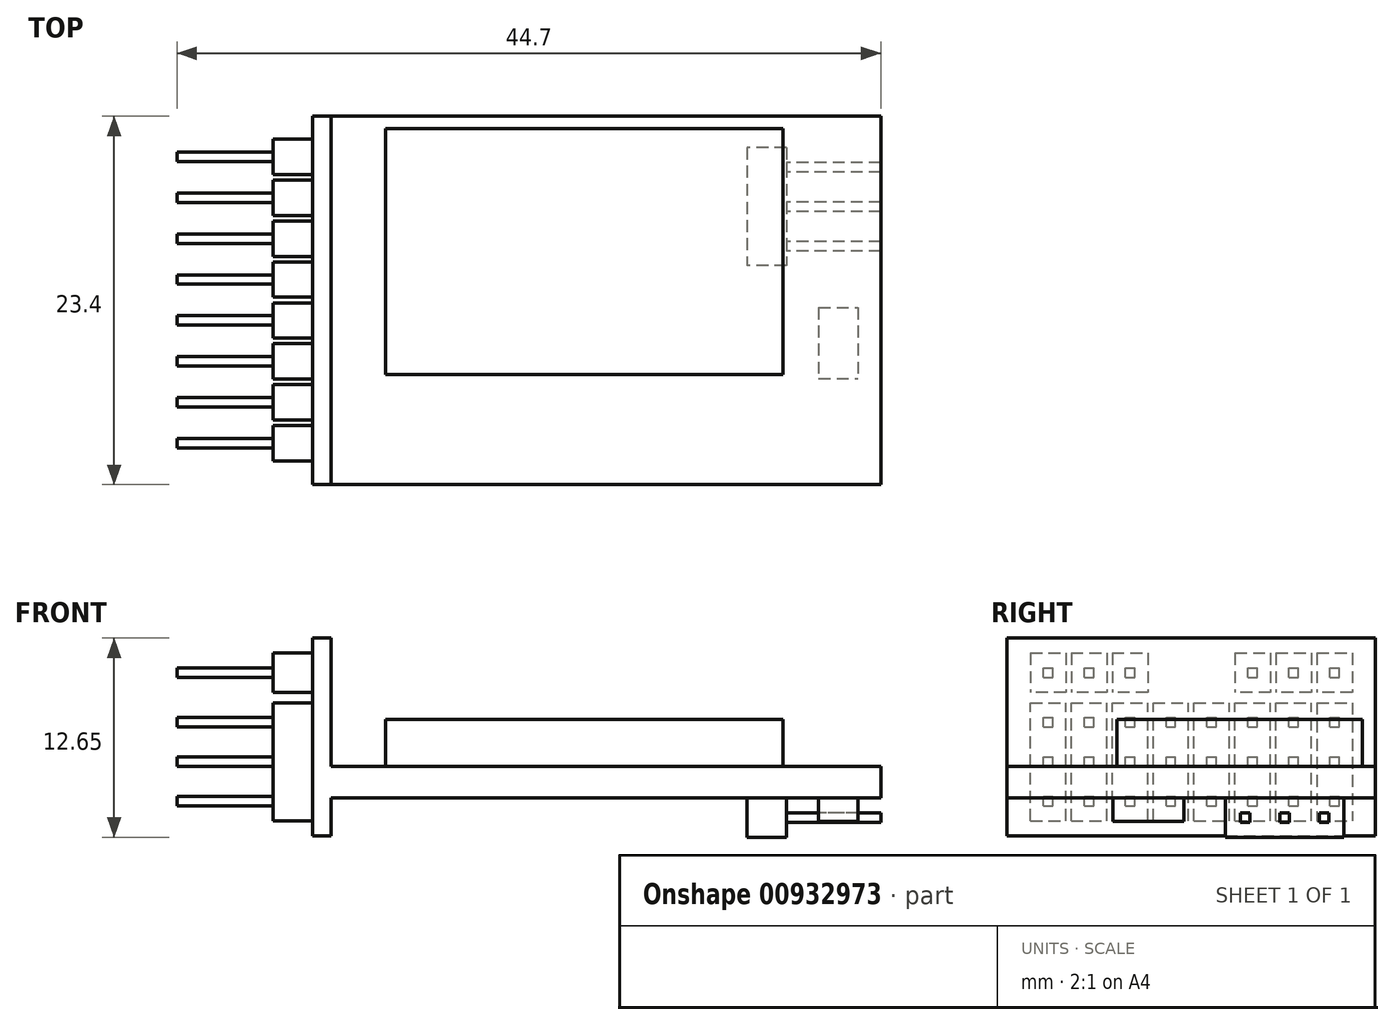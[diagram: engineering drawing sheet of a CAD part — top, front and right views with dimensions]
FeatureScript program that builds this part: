
annotation { "Feature Type Name" : "Feature", "Feature Type Description" : "" }
export const myFeature = defineFeature(function(context is Context, id is Id, definition is map)
    precondition{}
    {
        {
            var Q0;
            Q0=qCreatedBy(makeId("Top.planeOp"),FACE);
            var sketch = newSketch(context, id + "F0", { "sketchPlane" : qUnion([Q0])});
            skLineSegment(sketch, "E0.bottom", {"start": v(0, 0) * mm, "end": v(36.1, 0) * mm});
            skLineSegment(sketch, "E0.top", {"start": v(0, 23.4) * mm, "end": v(36.1, 23.4) * mm});
            skLineSegment(sketch, "E0.left", {"start": v(0, 0) * mm, "end": v(0, 23.4) * mm});
            skLineSegment(sketch, "E0.right", {"start": v(36.1, 0) * mm, "end": v(36.1, 23.4) * mm});
            skLineSegment(sketch, "E1.bottom", {"start": v(4.65, 22.6) * mm, "end": v(29.9, 22.6) * mm});
            skLineSegment(sketch, "E1.top", {"start": v(4.65, 7) * mm, "end": v(29.9, 7) * mm});
            skLineSegment(sketch, "E1.left", {"start": v(4.65, 22.6) * mm, "end": v(4.65, 7) * mm});
            skLineSegment(sketch, "E1.right", {"start": v(29.9, 22.6) * mm, "end": v(29.9, 7) * mm});
            skSolve(sketch);
        }
        {
            var Q0;
            Q0=makeQuery(id+"F0.imprint","IMPRINT",FACE,{"disambiguationData":[TD([[makeQuery(id+"F0.imprint","IMPRINT",EDGE,{"derivedFrom":sQuery(id+"F0.wireOp",EDGE,"E0.bottom")}),1.0]])]});
            extrude(context, id + "F1", {"entities" : qUnion([Q0]), "depth" : 2 * mm, "offsetDistance" : 25 * mm});
        }
        {
            var Q0;
            Q0=makeQuery(id+"F1.opExtrude","SWEPT_FACE",FACE,{"disambiguationData":[OSD([sQuery(id+"F0.wireOp",EDGE,"E0.left")])]});
            var sketch = newSketch(context, id + "F2", { "sketchPlane" : qUnion([Q0])});
            skLineSegment(sketch, "E2.bottom", {"start": v(0, -2.4) * mm, "end": v(-23.4, -2.4) * mm});
            skLineSegment(sketch, "E2.top", {"start": v(0, 10.15) * mm, "end": v(-23.4, 10.15) * mm});
            skLineSegment(sketch, "E2.left", {"start": v(0, -2.4) * mm, "end": v(0, 10.15) * mm});
            skLineSegment(sketch, "E2.right", {"start": v(-23.4, -2.4) * mm, "end": v(-23.4, 10.15) * mm});
            skPoint(sketch, "E3.0", {"position": v(0, 2) * mm});
            skPoint(sketch, "E4.0", {"position": v(0, 0) * mm});
            skLineSegment(sketch, "E5", {"start": v(-11.7, 10.15) * mm, "end": v(-11.7, -2.4) * mm, "construction": true});
            skLineSegment(sketch, "E6.bottom", {"start": v(-1.45, 9.2) * mm, "end": v(-21.95, 9.2) * mm});
            skLineSegment(sketch, "E6.top", {"start": v(-1.45, -1.45) * mm, "end": v(-21.95, -1.45) * mm});
            skLineSegment(sketch, "E6.left", {"start": v(-1.45, 9.2) * mm, "end": v(-1.45, -1.45) * mm});
            skLineSegment(sketch, "E6.right", {"start": v(-21.95, 9.2) * mm, "end": v(-21.95, -1.45) * mm});
            skPoint(sketch, "E6.middle", {"position": v(-11.7, 3.87) * mm});
            skLineSegment(sketch, "E7", {"start": v(-19.7, 9.2) * mm, "end": v(-19.7, -1.45) * mm});
            skLineSegment(sketch, "E8.bottom", {"start": v(-21.95, 9.2) * mm, "end": v(-19.7, 9.2) * mm});
            skLineSegment(sketch, "E8.top", {"start": v(-21.95, 6.2) * mm, "end": v(-19.7, 6.2) * mm});
            skLineSegment(sketch, "E8.left", {"start": v(-21.95, 9.2) * mm, "end": v(-21.95, 6.2) * mm});
            skLineSegment(sketch, "E8.right", {"start": v(-19.7, 9.2) * mm, "end": v(-19.7, 6.2) * mm});
            skLineSegment(sketch, "E9.bottom", {"start": v(-19.7, -1.45) * mm, "end": v(-21.95, -1.45) * mm});
            skLineSegment(sketch, "E9.top", {"start": v(-19.7, 1.05) * mm, "end": v(-21.95, 1.05) * mm});
            skLineSegment(sketch, "E9.left", {"start": v(-19.7, -1.45) * mm, "end": v(-19.7, 1.05) * mm});
            skLineSegment(sketch, "E9.right", {"start": v(-21.95, -1.45) * mm, "end": v(-21.95, 1.05) * mm});
            skLineSegment(sketch, "E10.top", {"start": v(-19.7, 3.55) * mm, "end": v(-21.95, 3.55) * mm});
            skLineSegment(sketch, "E10.left", {"start": v(-19.7, 1.05) * mm, "end": v(-19.7, 3.55) * mm});
            skLineSegment(sketch, "E10.right", {"start": v(-21.95, 1.05) * mm, "end": v(-21.95, 3.55) * mm});
            skLineSegment(sketch, "E11.top", {"start": v(-19.7, 6.05) * mm, "end": v(-21.95, 6.05) * mm});
            skLineSegment(sketch, "E11.left", {"start": v(-19.7, 3.55) * mm, "end": v(-19.7, 6.05) * mm});
            skLineSegment(sketch, "E11.right", {"start": v(-21.95, 3.55) * mm, "end": v(-21.95, 6.05) * mm});
            skLineSegment(sketch, "E12.top", {"start": v(-21.95, 6.7) * mm, "end": v(-19.7, 6.7) * mm});
            skLineSegment(sketch, "E12.left", {"start": v(-21.95, 9.2) * mm, "end": v(-21.95, 6.7) * mm});
            skLineSegment(sketch, "E12.right", {"start": v(-19.7, 9.2) * mm, "end": v(-19.7, 6.7) * mm});
            skLineSegment(sketch, "E13", {"start": v(-20.83, 9.2) * mm, "end": v(-20.83, 6.7) * mm, "construction": true});
            skLineSegment(sketch, "E14", {"start": v(-20.83, 6.05) * mm, "end": v(-20.83, 3.55) * mm, "construction": true});
            skLineSegment(sketch, "E15", {"start": v(-20.83, 3.55) * mm, "end": v(-20.83, 1.05) * mm, "construction": true});
            skLineSegment(sketch, "E16", {"start": v(-20.83, 1.05) * mm, "end": v(-20.83, -1.45) * mm, "construction": true});
            skLineSegment(sketch, "E17.bottom", {"start": v(-20.53, 4.5) * mm, "end": v(-21.13, 4.5) * mm});
            skLineSegment(sketch, "E17.top", {"start": v(-20.53, 5.1) * mm, "end": v(-21.13, 5.1) * mm});
            skLineSegment(sketch, "E17.left", {"start": v(-20.53, 4.5) * mm, "end": v(-20.53, 5.1) * mm});
            skLineSegment(sketch, "E17.right", {"start": v(-21.13, 4.5) * mm, "end": v(-21.13, 5.1) * mm});
            skPoint(sketch, "E17.middle", {"position": v(-20.83, 4.8) * mm});
            skLineSegment(sketch, "E18.bottom", {"start": v(-20.53, 2) * mm, "end": v(-21.13, 2) * mm});
            skLineSegment(sketch, "E18.top", {"start": v(-20.53, 2.6) * mm, "end": v(-21.13, 2.6) * mm});
            skLineSegment(sketch, "E18.left", {"start": v(-20.53, 2) * mm, "end": v(-20.53, 2.6) * mm});
            skLineSegment(sketch, "E18.right", {"start": v(-21.13, 2) * mm, "end": v(-21.13, 2.6) * mm});
            skPoint(sketch, "E18.middle", {"position": v(-20.83, 2.3) * mm});
            skLineSegment(sketch, "E19.bottom", {"start": v(-20.53, -0.5) * mm, "end": v(-21.13, -0.5) * mm});
            skLineSegment(sketch, "E19.top", {"start": v(-20.53, 0.1) * mm, "end": v(-21.13, 0.1) * mm});
            skLineSegment(sketch, "E19.left", {"start": v(-20.53, -0.5) * mm, "end": v(-20.53, 0.1) * mm});
            skLineSegment(sketch, "E19.right", {"start": v(-21.13, -0.5) * mm, "end": v(-21.13, 0.1) * mm});
            skPoint(sketch, "E19.middle", {"position": v(-20.83, -0.2) * mm});
            skLineSegment(sketch, "E20.bottom", {"start": v(-20.53, 7.65) * mm, "end": v(-21.13, 7.65) * mm});
            skLineSegment(sketch, "E20.top", {"start": v(-20.53, 8.25) * mm, "end": v(-21.13, 8.25) * mm});
            skLineSegment(sketch, "E20.left", {"start": v(-20.53, 7.65) * mm, "end": v(-20.53, 8.25) * mm});
            skLineSegment(sketch, "E20.right", {"start": v(-21.13, 7.65) * mm, "end": v(-21.13, 8.25) * mm});
            skPoint(sketch, "E20.middle", {"position": v(-20.83, 7.95) * mm});
            skLineSegment(sketch, "E21.1.0.0", {"start": v(-17.1, 9.2) * mm, "end": v(-17.1, 6.7) * mm});
            skLineSegment(sketch, "E21.1.0.1", {"start": v(-17.1, 1.05) * mm, "end": v(-17.1, 3.55) * mm});
            skLineSegment(sketch, "E21.1.0.2", {"start": v(-18.23, 9.2) * mm, "end": v(-18.23, 6.7) * mm, "construction": true});
            skLineSegment(sketch, "E21.1.0.3", {"start": v(-18.22, 3.55) * mm, "end": v(-18.22, 1.05) * mm, "construction": true});
            skLineSegment(sketch, "E21.1.0.4", {"start": v(-18.22, 1.05) * mm, "end": v(-18.22, -1.45) * mm, "construction": true});
            skLineSegment(sketch, "E21.1.0.5", {"start": v(-17.1, 3.55) * mm, "end": v(-19.35, 3.55) * mm});
            skPoint(sketch, "E21.1.0.6", {"position": v(-18.22, 2.3) * mm});
            skLineSegment(sketch, "E21.1.0.7", {"start": v(-19.35, 3.55) * mm, "end": v(-19.35, 6.05) * mm});
            skLineSegment(sketch, "E21.1.0.8", {"start": v(-17.1, 1.05) * mm, "end": v(-19.35, 1.05) * mm});
            skLineSegment(sketch, "E21.1.0.9", {"start": v(-19.35, 6.2) * mm, "end": v(-17.1, 6.2) * mm});
            skLineSegment(sketch, "E21.1.0.10", {"start": v(-18.22, 6.05) * mm, "end": v(-18.22, 3.55) * mm, "construction": true});
            skPoint(sketch, "E21.1.0.11", {"position": v(-18.22, -0.2) * mm});
            skPoint(sketch, "E21.1.0.12", {"position": v(-18.22, 7.95) * mm});
            skLineSegment(sketch, "E21.1.0.13", {"start": v(-17.1, 3.55) * mm, "end": v(-17.1, 6.05) * mm});
            skLineSegment(sketch, "E21.1.0.14", {"start": v(-19.35, 9.2) * mm, "end": v(-17.1, 9.2) * mm});
            skLineSegment(sketch, "E21.1.0.15", {"start": v(-19.35, 6.7) * mm, "end": v(-17.1, 6.7) * mm});
            skLineSegment(sketch, "E21.1.0.16", {"start": v(-19.35, 9.2) * mm, "end": v(-19.35, 6.7) * mm});
            skLineSegment(sketch, "E21.1.0.17", {"start": v(-19.35, -1.45) * mm, "end": v(-19.35, 1.05) * mm});
            skLineSegment(sketch, "E21.1.0.18", {"start": v(-19.35, 1.05) * mm, "end": v(-19.35, 3.55) * mm});
            skLineSegment(sketch, "E21.1.0.19", {"start": v(-17.1, -1.45) * mm, "end": v(-17.1, 1.05) * mm});
            skLineSegment(sketch, "E21.1.0.20", {"start": v(-17.1, -1.45) * mm, "end": v(-19.35, -1.45) * mm});
            skLineSegment(sketch, "E21.1.0.21", {"start": v(-17.1, 6.05) * mm, "end": v(-19.35, 6.05) * mm});
            skPoint(sketch, "E21.1.0.22", {"position": v(-18.22, 4.8) * mm});
            skLineSegment(sketch, "E21.1.0.23", {"start": v(-17.1, 9.2) * mm, "end": v(-17.1, -1.45) * mm});
            skLineSegment(sketch, "E21.1.0.24", {"start": v(-17.1, 9.2) * mm, "end": v(-17.1, 6.2) * mm});
            skLineSegment(sketch, "E21.1.0.25", {"start": v(-19.35, 9.2) * mm, "end": v(-19.35, -1.45) * mm});
            skLineSegment(sketch, "E21.1.0.26", {"start": v(-19.35, 9.2) * mm, "end": v(-19.35, 6.2) * mm});
            skLineSegment(sketch, "E21.1.0.27", {"start": v(-17.1, 1.05) * mm, "end": v(-19.35, 1.05) * mm});
            skLineSegment(sketch, "E21.1.0.28", {"start": v(-17.1, 3.55) * mm, "end": v(-19.35, 3.55) * mm});
            skLineSegment(sketch, "E21.1.0.29", {"start": v(-19.35, 9.2) * mm, "end": v(-17.1, 9.2) * mm});
            skLineSegment(sketch, "E21.1.0.30", {"start": v(-17.93, 2) * mm, "end": v(-18.53, 2) * mm});
            skLineSegment(sketch, "E21.1.0.31", {"start": v(-18.52, 4.5) * mm, "end": v(-18.52, 5.1) * mm});
            skLineSegment(sketch, "E21.1.0.32", {"start": v(-17.93, 2.6) * mm, "end": v(-18.53, 2.6) * mm});
            skLineSegment(sketch, "E21.1.0.33", {"start": v(-17.93, -0.5) * mm, "end": v(-18.52, -0.5) * mm});
            skLineSegment(sketch, "E21.1.0.34", {"start": v(-17.93, 7.65) * mm, "end": v(-17.93, 8.25) * mm});
            skLineSegment(sketch, "E21.1.0.35", {"start": v(-17.93, 2) * mm, "end": v(-17.93, 2.6) * mm});
            skLineSegment(sketch, "E21.1.0.36", {"start": v(-18.52, -0.5) * mm, "end": v(-18.52, 0.1) * mm});
            skLineSegment(sketch, "E21.1.0.37", {"start": v(-17.93, -0.5) * mm, "end": v(-17.93, 0.1) * mm});
            skLineSegment(sketch, "E21.1.0.38", {"start": v(-17.93, 7.65) * mm, "end": v(-18.52, 7.65) * mm});
            skLineSegment(sketch, "E21.1.0.39", {"start": v(-18.53, 2) * mm, "end": v(-18.53, 2.6) * mm});
            skLineSegment(sketch, "E21.1.0.40", {"start": v(-18.52, 7.65) * mm, "end": v(-18.52, 8.25) * mm});
            skLineSegment(sketch, "E21.1.0.41", {"start": v(-17.93, 4.5) * mm, "end": v(-18.52, 4.5) * mm});
            skLineSegment(sketch, "E21.1.0.42", {"start": v(-17.93, 5.1) * mm, "end": v(-18.52, 5.1) * mm});
            skLineSegment(sketch, "E21.1.0.43", {"start": v(-17.93, 8.25) * mm, "end": v(-18.52, 8.25) * mm});
            skLineSegment(sketch, "E21.1.0.44", {"start": v(-17.93, 4.5) * mm, "end": v(-17.93, 5.1) * mm});
            skLineSegment(sketch, "E21.1.0.45", {"start": v(-17.93, 0.1) * mm, "end": v(-18.52, 0.1) * mm});
            skLineSegment(sketch, "E21.2.0.0", {"start": v(-14.5, 9.2) * mm, "end": v(-14.5, 6.7) * mm});
            skLineSegment(sketch, "E21.2.0.1", {"start": v(-14.5, 1.05) * mm, "end": v(-14.5, 3.55) * mm});
            skLineSegment(sketch, "E21.2.0.2", {"start": v(-15.63, 9.2) * mm, "end": v(-15.63, 6.7) * mm, "construction": true});
            skLineSegment(sketch, "E21.2.0.3", {"start": v(-15.62, 3.55) * mm, "end": v(-15.62, 1.05) * mm, "construction": true});
            skLineSegment(sketch, "E21.2.0.4", {"start": v(-15.62, 1.05) * mm, "end": v(-15.62, -1.45) * mm, "construction": true});
            skLineSegment(sketch, "E21.2.0.5", {"start": v(-14.5, 3.55) * mm, "end": v(-16.75, 3.55) * mm});
            skPoint(sketch, "E21.2.0.6", {"position": v(-15.62, 2.3) * mm});
            skLineSegment(sketch, "E21.2.0.7", {"start": v(-16.75, 3.55) * mm, "end": v(-16.75, 6.05) * mm});
            skLineSegment(sketch, "E21.2.0.8", {"start": v(-14.5, 1.05) * mm, "end": v(-16.75, 1.05) * mm});
            skLineSegment(sketch, "E21.2.0.9", {"start": v(-16.75, 6.2) * mm, "end": v(-14.5, 6.2) * mm});
            skLineSegment(sketch, "E21.2.0.10", {"start": v(-15.62, 6.05) * mm, "end": v(-15.62, 3.55) * mm, "construction": true});
            skPoint(sketch, "E21.2.0.11", {"position": v(-15.62, -0.2) * mm});
            skPoint(sketch, "E21.2.0.12", {"position": v(-15.62, 7.95) * mm});
            skLineSegment(sketch, "E21.2.0.13", {"start": v(-14.5, 3.55) * mm, "end": v(-14.5, 6.05) * mm});
            skLineSegment(sketch, "E21.2.0.14", {"start": v(-16.75, 9.2) * mm, "end": v(-14.5, 9.2) * mm});
            skLineSegment(sketch, "E21.2.0.15", {"start": v(-16.75, 6.7) * mm, "end": v(-14.5, 6.7) * mm});
            skLineSegment(sketch, "E21.2.0.16", {"start": v(-16.75, 9.2) * mm, "end": v(-16.75, 6.7) * mm});
            skLineSegment(sketch, "E21.2.0.17", {"start": v(-16.75, -1.45) * mm, "end": v(-16.75, 1.05) * mm});
            skLineSegment(sketch, "E21.2.0.18", {"start": v(-16.75, 1.05) * mm, "end": v(-16.75, 3.55) * mm});
            skLineSegment(sketch, "E21.2.0.19", {"start": v(-14.5, -1.45) * mm, "end": v(-14.5, 1.05) * mm});
            skLineSegment(sketch, "E21.2.0.20", {"start": v(-14.5, -1.45) * mm, "end": v(-16.75, -1.45) * mm});
            skLineSegment(sketch, "E21.2.0.21", {"start": v(-14.5, 6.05) * mm, "end": v(-16.75, 6.05) * mm});
            skPoint(sketch, "E21.2.0.22", {"position": v(-15.62, 4.8) * mm});
            skLineSegment(sketch, "E21.2.0.23", {"start": v(-14.5, 9.2) * mm, "end": v(-14.5, -1.45) * mm});
            skLineSegment(sketch, "E21.2.0.24", {"start": v(-14.5, 9.2) * mm, "end": v(-14.5, 6.2) * mm});
            skLineSegment(sketch, "E21.2.0.25", {"start": v(-16.75, 9.2) * mm, "end": v(-16.75, -1.45) * mm});
            skLineSegment(sketch, "E21.2.0.26", {"start": v(-16.75, 9.2) * mm, "end": v(-16.75, 6.2) * mm});
            skLineSegment(sketch, "E21.2.0.27", {"start": v(-14.5, 1.05) * mm, "end": v(-16.75, 1.05) * mm});
            skLineSegment(sketch, "E21.2.0.28", {"start": v(-14.5, 3.55) * mm, "end": v(-16.75, 3.55) * mm});
            skLineSegment(sketch, "E21.2.0.29", {"start": v(-16.75, 9.2) * mm, "end": v(-14.5, 9.2) * mm});
            skLineSegment(sketch, "E21.2.0.30", {"start": v(-15.33, 2) * mm, "end": v(-15.93, 2) * mm});
            skLineSegment(sketch, "E21.2.0.31", {"start": v(-15.93, 4.5) * mm, "end": v(-15.93, 5.1) * mm});
            skLineSegment(sketch, "E21.2.0.32", {"start": v(-15.33, 2.6) * mm, "end": v(-15.93, 2.6) * mm});
            skLineSegment(sketch, "E21.2.0.33", {"start": v(-15.33, -0.5) * mm, "end": v(-15.93, -0.5) * mm});
            skLineSegment(sketch, "E21.2.0.34", {"start": v(-15.33, 7.65) * mm, "end": v(-15.33, 8.25) * mm});
            skLineSegment(sketch, "E21.2.0.35", {"start": v(-15.33, 2) * mm, "end": v(-15.33, 2.6) * mm});
            skLineSegment(sketch, "E21.2.0.36", {"start": v(-15.93, -0.5) * mm, "end": v(-15.93, 0.1) * mm});
            skLineSegment(sketch, "E21.2.0.37", {"start": v(-15.33, -0.5) * mm, "end": v(-15.33, 0.1) * mm});
            skLineSegment(sketch, "E21.2.0.38", {"start": v(-15.33, 7.65) * mm, "end": v(-15.93, 7.65) * mm});
            skLineSegment(sketch, "E21.2.0.39", {"start": v(-15.93, 2) * mm, "end": v(-15.93, 2.6) * mm});
            skLineSegment(sketch, "E21.2.0.40", {"start": v(-15.93, 7.65) * mm, "end": v(-15.93, 8.25) * mm});
            skLineSegment(sketch, "E21.2.0.41", {"start": v(-15.33, 4.5) * mm, "end": v(-15.93, 4.5) * mm});
            skLineSegment(sketch, "E21.2.0.42", {"start": v(-15.33, 5.1) * mm, "end": v(-15.93, 5.1) * mm});
            skLineSegment(sketch, "E21.2.0.43", {"start": v(-15.33, 8.25) * mm, "end": v(-15.93, 8.25) * mm});
            skLineSegment(sketch, "E21.2.0.44", {"start": v(-15.33, 4.5) * mm, "end": v(-15.33, 5.1) * mm});
            skLineSegment(sketch, "E21.2.0.45", {"start": v(-15.33, 0.1) * mm, "end": v(-15.93, 0.1) * mm});
            skLineSegment(sketch, "E21.3.0.0", {"start": v(-11.9, 9.2) * mm, "end": v(-11.9, 6.7) * mm});
            skLineSegment(sketch, "E21.3.0.1", {"start": v(-11.9, 1.05) * mm, "end": v(-11.9, 3.55) * mm});
            skLineSegment(sketch, "E21.3.0.2", {"start": v(-13.03, 9.2) * mm, "end": v(-13.03, 6.7) * mm, "construction": true});
            skLineSegment(sketch, "E21.3.0.3", {"start": v(-13.02, 3.55) * mm, "end": v(-13.02, 1.05) * mm, "construction": true});
            skLineSegment(sketch, "E21.3.0.4", {"start": v(-13.02, 1.05) * mm, "end": v(-13.02, -1.45) * mm, "construction": true});
            skLineSegment(sketch, "E21.3.0.5", {"start": v(-11.9, 3.55) * mm, "end": v(-14.15, 3.55) * mm});
            skPoint(sketch, "E21.3.0.6", {"position": v(-13.02, 2.3) * mm});
            skLineSegment(sketch, "E21.3.0.7", {"start": v(-14.15, 3.55) * mm, "end": v(-14.15, 6.05) * mm});
            skLineSegment(sketch, "E21.3.0.8", {"start": v(-11.9, 1.05) * mm, "end": v(-14.15, 1.05) * mm});
            skLineSegment(sketch, "E21.3.0.9", {"start": v(-14.15, 6.2) * mm, "end": v(-11.9, 6.2) * mm});
            skLineSegment(sketch, "E21.3.0.10", {"start": v(-13.02, 6.05) * mm, "end": v(-13.02, 3.55) * mm, "construction": true});
            skPoint(sketch, "E21.3.0.11", {"position": v(-13.02, -0.2) * mm});
            skPoint(sketch, "E21.3.0.12", {"position": v(-13.02, 7.95) * mm});
            skLineSegment(sketch, "E21.3.0.13", {"start": v(-11.9, 3.55) * mm, "end": v(-11.9, 6.05) * mm});
            skLineSegment(sketch, "E21.3.0.14", {"start": v(-14.15, 9.2) * mm, "end": v(-11.9, 9.2) * mm});
            skLineSegment(sketch, "E21.3.0.15", {"start": v(-14.15, 6.7) * mm, "end": v(-11.9, 6.7) * mm});
            skLineSegment(sketch, "E21.3.0.16", {"start": v(-14.15, 9.2) * mm, "end": v(-14.15, 6.7) * mm});
            skLineSegment(sketch, "E21.3.0.17", {"start": v(-14.15, -1.45) * mm, "end": v(-14.15, 1.05) * mm});
            skLineSegment(sketch, "E21.3.0.18", {"start": v(-14.15, 1.05) * mm, "end": v(-14.15, 3.55) * mm});
            skLineSegment(sketch, "E21.3.0.19", {"start": v(-11.9, -1.45) * mm, "end": v(-11.9, 1.05) * mm});
            skLineSegment(sketch, "E21.3.0.20", {"start": v(-11.9, -1.45) * mm, "end": v(-14.15, -1.45) * mm});
            skLineSegment(sketch, "E21.3.0.21", {"start": v(-11.9, 6.05) * mm, "end": v(-14.15, 6.05) * mm});
            skPoint(sketch, "E21.3.0.22", {"position": v(-13.02, 4.8) * mm});
            skLineSegment(sketch, "E21.3.0.23", {"start": v(-11.9, 9.2) * mm, "end": v(-11.9, -1.45) * mm});
            skLineSegment(sketch, "E21.3.0.24", {"start": v(-11.9, 9.2) * mm, "end": v(-11.9, 6.2) * mm});
            skLineSegment(sketch, "E21.3.0.25", {"start": v(-14.15, 9.2) * mm, "end": v(-14.15, -1.45) * mm});
            skLineSegment(sketch, "E21.3.0.26", {"start": v(-14.15, 9.2) * mm, "end": v(-14.15, 6.2) * mm});
            skLineSegment(sketch, "E21.3.0.27", {"start": v(-11.9, 1.05) * mm, "end": v(-14.15, 1.05) * mm});
            skLineSegment(sketch, "E21.3.0.28", {"start": v(-11.9, 3.55) * mm, "end": v(-14.15, 3.55) * mm});
            skLineSegment(sketch, "E21.3.0.29", {"start": v(-14.15, 9.2) * mm, "end": v(-11.9, 9.2) * mm});
            skLineSegment(sketch, "E21.3.0.30", {"start": v(-12.73, 2) * mm, "end": v(-13.33, 2) * mm});
            skLineSegment(sketch, "E21.3.0.31", {"start": v(-13.32, 4.5) * mm, "end": v(-13.32, 5.1) * mm});
            skLineSegment(sketch, "E21.3.0.32", {"start": v(-12.73, 2.6) * mm, "end": v(-13.33, 2.6) * mm});
            skLineSegment(sketch, "E21.3.0.33", {"start": v(-12.72, -0.5) * mm, "end": v(-13.32, -0.5) * mm});
            skLineSegment(sketch, "E21.3.0.34", {"start": v(-12.72, 7.65) * mm, "end": v(-12.72, 8.25) * mm});
            skLineSegment(sketch, "E21.3.0.35", {"start": v(-12.73, 2) * mm, "end": v(-12.73, 2.6) * mm});
            skLineSegment(sketch, "E21.3.0.36", {"start": v(-13.32, -0.5) * mm, "end": v(-13.32, 0.1) * mm});
            skLineSegment(sketch, "E21.3.0.37", {"start": v(-12.72, -0.5) * mm, "end": v(-12.72, 0.1) * mm});
            skLineSegment(sketch, "E21.3.0.38", {"start": v(-12.72, 7.65) * mm, "end": v(-13.32, 7.65) * mm});
            skLineSegment(sketch, "E21.3.0.39", {"start": v(-13.33, 2) * mm, "end": v(-13.33, 2.6) * mm});
            skLineSegment(sketch, "E21.3.0.40", {"start": v(-13.32, 7.65) * mm, "end": v(-13.32, 8.25) * mm});
            skLineSegment(sketch, "E21.3.0.41", {"start": v(-12.72, 4.5) * mm, "end": v(-13.32, 4.5) * mm});
            skLineSegment(sketch, "E21.3.0.42", {"start": v(-12.72, 5.1) * mm, "end": v(-13.32, 5.1) * mm});
            skLineSegment(sketch, "E21.3.0.43", {"start": v(-12.72, 8.25) * mm, "end": v(-13.32, 8.25) * mm});
            skLineSegment(sketch, "E21.3.0.44", {"start": v(-12.72, 4.5) * mm, "end": v(-12.72, 5.1) * mm});
            skLineSegment(sketch, "E21.3.0.45", {"start": v(-12.72, 0.1) * mm, "end": v(-13.32, 0.1) * mm});
            skLineSegment(sketch, "E21.4.0.0", {"start": v(-9.3, 9.2) * mm, "end": v(-9.3, 6.7) * mm});
            skLineSegment(sketch, "E21.4.0.1", {"start": v(-9.3, 1.05) * mm, "end": v(-9.3, 3.55) * mm});
            skLineSegment(sketch, "E21.4.0.2", {"start": v(-10.43, 9.2) * mm, "end": v(-10.43, 6.7) * mm, "construction": true});
            skLineSegment(sketch, "E21.4.0.3", {"start": v(-10.42, 3.55) * mm, "end": v(-10.42, 1.05) * mm, "construction": true});
            skLineSegment(sketch, "E21.4.0.4", {"start": v(-10.42, 1.05) * mm, "end": v(-10.42, -1.45) * mm, "construction": true});
            skLineSegment(sketch, "E21.4.0.5", {"start": v(-9.3, 3.55) * mm, "end": v(-11.55, 3.55) * mm});
            skPoint(sketch, "E21.4.0.6", {"position": v(-10.42, 2.3) * mm});
            skLineSegment(sketch, "E21.4.0.7", {"start": v(-11.55, 3.55) * mm, "end": v(-11.55, 6.05) * mm});
            skLineSegment(sketch, "E21.4.0.8", {"start": v(-9.3, 1.05) * mm, "end": v(-11.55, 1.05) * mm});
            skLineSegment(sketch, "E21.4.0.9", {"start": v(-11.55, 6.2) * mm, "end": v(-9.3, 6.2) * mm});
            skLineSegment(sketch, "E21.4.0.10", {"start": v(-10.42, 6.05) * mm, "end": v(-10.42, 3.55) * mm, "construction": true});
            skPoint(sketch, "E21.4.0.11", {"position": v(-10.42, -0.2) * mm});
            skPoint(sketch, "E21.4.0.12", {"position": v(-10.42, 7.95) * mm});
            skLineSegment(sketch, "E21.4.0.13", {"start": v(-9.3, 3.55) * mm, "end": v(-9.3, 6.05) * mm});
            skLineSegment(sketch, "E21.4.0.14", {"start": v(-11.55, 9.2) * mm, "end": v(-9.3, 9.2) * mm});
            skLineSegment(sketch, "E21.4.0.15", {"start": v(-11.55, 6.7) * mm, "end": v(-9.3, 6.7) * mm});
            skLineSegment(sketch, "E21.4.0.16", {"start": v(-11.55, 9.2) * mm, "end": v(-11.55, 6.7) * mm});
            skLineSegment(sketch, "E21.4.0.17", {"start": v(-11.55, -1.45) * mm, "end": v(-11.55, 1.05) * mm});
            skLineSegment(sketch, "E21.4.0.18", {"start": v(-11.55, 1.05) * mm, "end": v(-11.55, 3.55) * mm});
            skLineSegment(sketch, "E21.4.0.19", {"start": v(-9.3, -1.45) * mm, "end": v(-9.3, 1.05) * mm});
            skLineSegment(sketch, "E21.4.0.20", {"start": v(-9.3, -1.45) * mm, "end": v(-11.55, -1.45) * mm});
            skLineSegment(sketch, "E21.4.0.21", {"start": v(-9.3, 6.05) * mm, "end": v(-11.55, 6.05) * mm});
            skPoint(sketch, "E21.4.0.22", {"position": v(-10.42, 4.8) * mm});
            skLineSegment(sketch, "E21.4.0.23", {"start": v(-9.3, 9.2) * mm, "end": v(-9.3, -1.45) * mm});
            skLineSegment(sketch, "E21.4.0.24", {"start": v(-9.3, 9.2) * mm, "end": v(-9.3, 6.2) * mm});
            skLineSegment(sketch, "E21.4.0.25", {"start": v(-11.55, 9.2) * mm, "end": v(-11.55, -1.45) * mm});
            skLineSegment(sketch, "E21.4.0.26", {"start": v(-11.55, 9.2) * mm, "end": v(-11.55, 6.2) * mm});
            skLineSegment(sketch, "E21.4.0.27", {"start": v(-9.3, 1.05) * mm, "end": v(-11.55, 1.05) * mm});
            skLineSegment(sketch, "E21.4.0.28", {"start": v(-9.3, 3.55) * mm, "end": v(-11.55, 3.55) * mm});
            skLineSegment(sketch, "E21.4.0.29", {"start": v(-11.55, 9.2) * mm, "end": v(-9.3, 9.2) * mm});
            skLineSegment(sketch, "E21.4.0.30", {"start": v(-10.13, 2) * mm, "end": v(-10.73, 2) * mm});
            skLineSegment(sketch, "E21.4.0.31", {"start": v(-10.72, 4.5) * mm, "end": v(-10.72, 5.1) * mm});
            skLineSegment(sketch, "E21.4.0.32", {"start": v(-10.13, 2.6) * mm, "end": v(-10.73, 2.6) * mm});
            skLineSegment(sketch, "E21.4.0.33", {"start": v(-10.12, -0.5) * mm, "end": v(-10.72, -0.5) * mm});
            skLineSegment(sketch, "E21.4.0.34", {"start": v(-10.12, 7.65) * mm, "end": v(-10.12, 8.25) * mm});
            skLineSegment(sketch, "E21.4.0.35", {"start": v(-10.13, 2) * mm, "end": v(-10.13, 2.6) * mm});
            skLineSegment(sketch, "E21.4.0.36", {"start": v(-10.72, -0.5) * mm, "end": v(-10.72, 0.1) * mm});
            skLineSegment(sketch, "E21.4.0.37", {"start": v(-10.12, -0.5) * mm, "end": v(-10.12, 0.1) * mm});
            skLineSegment(sketch, "E21.4.0.38", {"start": v(-10.12, 7.65) * mm, "end": v(-10.72, 7.65) * mm});
            skLineSegment(sketch, "E21.4.0.39", {"start": v(-10.73, 2) * mm, "end": v(-10.73, 2.6) * mm});
            skLineSegment(sketch, "E21.4.0.40", {"start": v(-10.72, 7.65) * mm, "end": v(-10.72, 8.25) * mm});
            skLineSegment(sketch, "E21.4.0.41", {"start": v(-10.12, 4.5) * mm, "end": v(-10.72, 4.5) * mm});
            skLineSegment(sketch, "E21.4.0.42", {"start": v(-10.12, 5.1) * mm, "end": v(-10.72, 5.1) * mm});
            skLineSegment(sketch, "E21.4.0.43", {"start": v(-10.12, 8.25) * mm, "end": v(-10.72, 8.25) * mm});
            skLineSegment(sketch, "E21.4.0.44", {"start": v(-10.12, 4.5) * mm, "end": v(-10.12, 5.1) * mm});
            skLineSegment(sketch, "E21.4.0.45", {"start": v(-10.12, 0.1) * mm, "end": v(-10.72, 0.1) * mm});
            skLineSegment(sketch, "E21.5.0.0", {"start": v(-6.7, 9.2) * mm, "end": v(-6.7, 6.7) * mm});
            skLineSegment(sketch, "E21.5.0.1", {"start": v(-6.7, 1.05) * mm, "end": v(-6.7, 3.55) * mm});
            skLineSegment(sketch, "E21.5.0.2", {"start": v(-7.83, 9.2) * mm, "end": v(-7.83, 6.7) * mm, "construction": true});
            skLineSegment(sketch, "E21.5.0.3", {"start": v(-7.82, 3.55) * mm, "end": v(-7.82, 1.05) * mm, "construction": true});
            skLineSegment(sketch, "E21.5.0.4", {"start": v(-7.82, 1.05) * mm, "end": v(-7.82, -1.45) * mm, "construction": true});
            skLineSegment(sketch, "E21.5.0.5", {"start": v(-6.7, 3.55) * mm, "end": v(-8.95, 3.55) * mm});
            skPoint(sketch, "E21.5.0.6", {"position": v(-7.82, 2.3) * mm});
            skLineSegment(sketch, "E21.5.0.7", {"start": v(-8.95, 3.55) * mm, "end": v(-8.95, 6.05) * mm});
            skLineSegment(sketch, "E21.5.0.8", {"start": v(-6.7, 1.05) * mm, "end": v(-8.95, 1.05) * mm});
            skLineSegment(sketch, "E21.5.0.9", {"start": v(-8.95, 6.2) * mm, "end": v(-6.7, 6.2) * mm});
            skLineSegment(sketch, "E21.5.0.10", {"start": v(-7.82, 6.05) * mm, "end": v(-7.82, 3.55) * mm, "construction": true});
            skPoint(sketch, "E21.5.0.11", {"position": v(-7.82, -0.2) * mm});
            skPoint(sketch, "E21.5.0.12", {"position": v(-7.82, 7.95) * mm});
            skLineSegment(sketch, "E21.5.0.13", {"start": v(-6.7, 3.55) * mm, "end": v(-6.7, 6.05) * mm});
            skLineSegment(sketch, "E21.5.0.14", {"start": v(-8.95, 9.2) * mm, "end": v(-6.7, 9.2) * mm});
            skLineSegment(sketch, "E21.5.0.15", {"start": v(-8.95, 6.7) * mm, "end": v(-6.7, 6.7) * mm});
            skLineSegment(sketch, "E21.5.0.16", {"start": v(-8.95, 9.2) * mm, "end": v(-8.95, 6.7) * mm});
            skLineSegment(sketch, "E21.5.0.17", {"start": v(-8.95, -1.45) * mm, "end": v(-8.95, 1.05) * mm});
            skLineSegment(sketch, "E21.5.0.18", {"start": v(-8.95, 1.05) * mm, "end": v(-8.95, 3.55) * mm});
            skLineSegment(sketch, "E21.5.0.19", {"start": v(-6.7, -1.45) * mm, "end": v(-6.7, 1.05) * mm});
            skLineSegment(sketch, "E21.5.0.20", {"start": v(-6.7, -1.45) * mm, "end": v(-8.95, -1.45) * mm});
            skLineSegment(sketch, "E21.5.0.21", {"start": v(-6.7, 6.05) * mm, "end": v(-8.95, 6.05) * mm});
            skPoint(sketch, "E21.5.0.22", {"position": v(-7.82, 4.8) * mm});
            skLineSegment(sketch, "E21.5.0.23", {"start": v(-6.7, 9.2) * mm, "end": v(-6.7, -1.45) * mm});
            skLineSegment(sketch, "E21.5.0.24", {"start": v(-6.7, 9.2) * mm, "end": v(-6.7, 6.2) * mm});
            skLineSegment(sketch, "E21.5.0.25", {"start": v(-8.95, 9.2) * mm, "end": v(-8.95, -1.45) * mm});
            skLineSegment(sketch, "E21.5.0.26", {"start": v(-8.95, 9.2) * mm, "end": v(-8.95, 6.2) * mm});
            skLineSegment(sketch, "E21.5.0.27", {"start": v(-6.7, 1.05) * mm, "end": v(-8.95, 1.05) * mm});
            skLineSegment(sketch, "E21.5.0.28", {"start": v(-6.7, 3.55) * mm, "end": v(-8.95, 3.55) * mm});
            skLineSegment(sketch, "E21.5.0.29", {"start": v(-8.95, 9.2) * mm, "end": v(-6.7, 9.2) * mm});
            skLineSegment(sketch, "E21.5.0.30", {"start": v(-7.53, 2) * mm, "end": v(-8.13, 2) * mm});
            skLineSegment(sketch, "E21.5.0.31", {"start": v(-8.12, 4.5) * mm, "end": v(-8.12, 5.1) * mm});
            skLineSegment(sketch, "E21.5.0.32", {"start": v(-7.53, 2.6) * mm, "end": v(-8.13, 2.6) * mm});
            skLineSegment(sketch, "E21.5.0.33", {"start": v(-7.53, -0.5) * mm, "end": v(-8.12, -0.5) * mm});
            skLineSegment(sketch, "E21.5.0.34", {"start": v(-7.53, 7.65) * mm, "end": v(-7.53, 8.25) * mm});
            skLineSegment(sketch, "E21.5.0.35", {"start": v(-7.53, 2) * mm, "end": v(-7.53, 2.6) * mm});
            skLineSegment(sketch, "E21.5.0.36", {"start": v(-8.12, -0.5) * mm, "end": v(-8.12, 0.1) * mm});
            skLineSegment(sketch, "E21.5.0.37", {"start": v(-7.53, -0.5) * mm, "end": v(-7.53, 0.1) * mm});
            skLineSegment(sketch, "E21.5.0.38", {"start": v(-7.53, 7.65) * mm, "end": v(-8.12, 7.65) * mm});
            skLineSegment(sketch, "E21.5.0.39", {"start": v(-8.13, 2) * mm, "end": v(-8.13, 2.6) * mm});
            skLineSegment(sketch, "E21.5.0.40", {"start": v(-8.12, 7.65) * mm, "end": v(-8.12, 8.25) * mm});
            skLineSegment(sketch, "E21.5.0.41", {"start": v(-7.53, 4.5) * mm, "end": v(-8.12, 4.5) * mm});
            skLineSegment(sketch, "E21.5.0.42", {"start": v(-7.53, 5.1) * mm, "end": v(-8.12, 5.1) * mm});
            skLineSegment(sketch, "E21.5.0.43", {"start": v(-7.53, 8.25) * mm, "end": v(-8.12, 8.25) * mm});
            skLineSegment(sketch, "E21.5.0.44", {"start": v(-7.53, 4.5) * mm, "end": v(-7.53, 5.1) * mm});
            skLineSegment(sketch, "E21.5.0.45", {"start": v(-7.53, 0.1) * mm, "end": v(-8.12, 0.1) * mm});
            skLineSegment(sketch, "E21.6.0.0", {"start": v(-4.1, 9.2) * mm, "end": v(-4.1, 6.7) * mm});
            skLineSegment(sketch, "E21.6.0.1", {"start": v(-4.1, 1.05) * mm, "end": v(-4.1, 3.55) * mm});
            skLineSegment(sketch, "E21.6.0.2", {"start": v(-5.23, 9.2) * mm, "end": v(-5.23, 6.7) * mm, "construction": true});
            skLineSegment(sketch, "E21.6.0.3", {"start": v(-5.22, 3.55) * mm, "end": v(-5.22, 1.05) * mm, "construction": true});
            skLineSegment(sketch, "E21.6.0.4", {"start": v(-5.22, 1.05) * mm, "end": v(-5.22, -1.45) * mm, "construction": true});
            skLineSegment(sketch, "E21.6.0.5", {"start": v(-4.1, 3.55) * mm, "end": v(-6.35, 3.55) * mm});
            skPoint(sketch, "E21.6.0.6", {"position": v(-5.22, 2.3) * mm});
            skLineSegment(sketch, "E21.6.0.7", {"start": v(-6.35, 3.55) * mm, "end": v(-6.35, 6.05) * mm});
            skLineSegment(sketch, "E21.6.0.8", {"start": v(-4.1, 1.05) * mm, "end": v(-6.35, 1.05) * mm});
            skLineSegment(sketch, "E21.6.0.9", {"start": v(-6.35, 6.2) * mm, "end": v(-4.1, 6.2) * mm});
            skLineSegment(sketch, "E21.6.0.10", {"start": v(-5.22, 6.05) * mm, "end": v(-5.22, 3.55) * mm, "construction": true});
            skPoint(sketch, "E21.6.0.11", {"position": v(-5.22, -0.2) * mm});
            skPoint(sketch, "E21.6.0.12", {"position": v(-5.22, 7.95) * mm});
            skLineSegment(sketch, "E21.6.0.13", {"start": v(-4.1, 3.55) * mm, "end": v(-4.1, 6.05) * mm});
            skLineSegment(sketch, "E21.6.0.14", {"start": v(-6.35, 9.2) * mm, "end": v(-4.1, 9.2) * mm});
            skLineSegment(sketch, "E21.6.0.15", {"start": v(-6.35, 6.7) * mm, "end": v(-4.1, 6.7) * mm});
            skLineSegment(sketch, "E21.6.0.16", {"start": v(-6.35, 9.2) * mm, "end": v(-6.35, 6.7) * mm});
            skLineSegment(sketch, "E21.6.0.17", {"start": v(-6.35, -1.45) * mm, "end": v(-6.35, 1.05) * mm});
            skLineSegment(sketch, "E21.6.0.18", {"start": v(-6.35, 1.05) * mm, "end": v(-6.35, 3.55) * mm});
            skLineSegment(sketch, "E21.6.0.19", {"start": v(-4.1, -1.45) * mm, "end": v(-4.1, 1.05) * mm});
            skLineSegment(sketch, "E21.6.0.20", {"start": v(-4.1, -1.45) * mm, "end": v(-6.35, -1.45) * mm});
            skLineSegment(sketch, "E21.6.0.21", {"start": v(-4.1, 6.05) * mm, "end": v(-6.35, 6.05) * mm});
            skPoint(sketch, "E21.6.0.22", {"position": v(-5.22, 4.8) * mm});
            skLineSegment(sketch, "E21.6.0.23", {"start": v(-4.1, 9.2) * mm, "end": v(-4.1, -1.45) * mm});
            skLineSegment(sketch, "E21.6.0.24", {"start": v(-4.1, 9.2) * mm, "end": v(-4.1, 6.2) * mm});
            skLineSegment(sketch, "E21.6.0.25", {"start": v(-6.35, 9.2) * mm, "end": v(-6.35, -1.45) * mm});
            skLineSegment(sketch, "E21.6.0.26", {"start": v(-6.35, 9.2) * mm, "end": v(-6.35, 6.2) * mm});
            skLineSegment(sketch, "E21.6.0.27", {"start": v(-4.1, 1.05) * mm, "end": v(-6.35, 1.05) * mm});
            skLineSegment(sketch, "E21.6.0.28", {"start": v(-4.1, 3.55) * mm, "end": v(-6.35, 3.55) * mm});
            skLineSegment(sketch, "E21.6.0.29", {"start": v(-6.35, 9.2) * mm, "end": v(-4.1, 9.2) * mm});
            skLineSegment(sketch, "E21.6.0.30", {"start": v(-4.93, 2) * mm, "end": v(-5.53, 2) * mm});
            skLineSegment(sketch, "E21.6.0.31", {"start": v(-5.52, 4.5) * mm, "end": v(-5.52, 5.1) * mm});
            skLineSegment(sketch, "E21.6.0.32", {"start": v(-4.93, 2.6) * mm, "end": v(-5.53, 2.6) * mm});
            skLineSegment(sketch, "E21.6.0.33", {"start": v(-4.93, -0.5) * mm, "end": v(-5.52, -0.5) * mm});
            skLineSegment(sketch, "E21.6.0.34", {"start": v(-4.92, 7.65) * mm, "end": v(-4.92, 8.25) * mm});
            skLineSegment(sketch, "E21.6.0.35", {"start": v(-4.93, 2) * mm, "end": v(-4.93, 2.6) * mm});
            skLineSegment(sketch, "E21.6.0.36", {"start": v(-5.52, -0.5) * mm, "end": v(-5.52, 0.1) * mm});
            skLineSegment(sketch, "E21.6.0.37", {"start": v(-4.92, -0.5) * mm, "end": v(-4.92, 0.1) * mm});
            skLineSegment(sketch, "E21.6.0.38", {"start": v(-4.93, 7.65) * mm, "end": v(-5.52, 7.65) * mm});
            skLineSegment(sketch, "E21.6.0.39", {"start": v(-5.53, 2) * mm, "end": v(-5.53, 2.6) * mm});
            skLineSegment(sketch, "E21.6.0.40", {"start": v(-5.52, 7.65) * mm, "end": v(-5.52, 8.25) * mm});
            skLineSegment(sketch, "E21.6.0.41", {"start": v(-4.92, 4.5) * mm, "end": v(-5.52, 4.5) * mm});
            skLineSegment(sketch, "E21.6.0.42", {"start": v(-4.92, 5.1) * mm, "end": v(-5.52, 5.1) * mm});
            skLineSegment(sketch, "E21.6.0.43", {"start": v(-4.92, 8.25) * mm, "end": v(-5.52, 8.25) * mm});
            skLineSegment(sketch, "E21.6.0.44", {"start": v(-4.92, 4.5) * mm, "end": v(-4.92, 5.1) * mm});
            skLineSegment(sketch, "E21.6.0.45", {"start": v(-4.92, 0.1) * mm, "end": v(-5.52, 0.1) * mm});
            skLineSegment(sketch, "E21.7.0.0", {"start": v(-1.5, 9.2) * mm, "end": v(-1.5, 6.7) * mm});
            skLineSegment(sketch, "E21.7.0.1", {"start": v(-1.5, 1.05) * mm, "end": v(-1.5, 3.55) * mm});
            skLineSegment(sketch, "E21.7.0.2", {"start": v(-2.63, 9.2) * mm, "end": v(-2.63, 6.7) * mm, "construction": true});
            skLineSegment(sketch, "E21.7.0.3", {"start": v(-2.62, 3.55) * mm, "end": v(-2.62, 1.05) * mm, "construction": true});
            skLineSegment(sketch, "E21.7.0.4", {"start": v(-2.62, 1.05) * mm, "end": v(-2.62, -1.45) * mm, "construction": true});
            skLineSegment(sketch, "E21.7.0.5", {"start": v(-1.5, 3.55) * mm, "end": v(-3.75, 3.55) * mm});
            skPoint(sketch, "E21.7.0.6", {"position": v(-2.62, 2.3) * mm});
            skLineSegment(sketch, "E21.7.0.7", {"start": v(-3.75, 3.55) * mm, "end": v(-3.75, 6.05) * mm});
            skLineSegment(sketch, "E21.7.0.8", {"start": v(-1.5, 1.05) * mm, "end": v(-3.75, 1.05) * mm});
            skLineSegment(sketch, "E21.7.0.9", {"start": v(-3.75, 6.2) * mm, "end": v(-1.5, 6.2) * mm});
            skLineSegment(sketch, "E21.7.0.10", {"start": v(-2.62, 6.05) * mm, "end": v(-2.62, 3.55) * mm, "construction": true});
            skPoint(sketch, "E21.7.0.11", {"position": v(-2.62, -0.2) * mm});
            skPoint(sketch, "E21.7.0.12", {"position": v(-2.62, 7.95) * mm});
            skLineSegment(sketch, "E21.7.0.13", {"start": v(-1.5, 3.55) * mm, "end": v(-1.5, 6.05) * mm});
            skLineSegment(sketch, "E21.7.0.14", {"start": v(-3.75, 9.2) * mm, "end": v(-1.5, 9.2) * mm});
            skLineSegment(sketch, "E21.7.0.15", {"start": v(-3.75, 6.7) * mm, "end": v(-1.5, 6.7) * mm});
            skLineSegment(sketch, "E21.7.0.16", {"start": v(-3.75, 9.2) * mm, "end": v(-3.75, 6.7) * mm});
            skLineSegment(sketch, "E21.7.0.17", {"start": v(-3.75, -1.45) * mm, "end": v(-3.75, 1.05) * mm});
            skLineSegment(sketch, "E21.7.0.18", {"start": v(-3.75, 1.05) * mm, "end": v(-3.75, 3.55) * mm});
            skLineSegment(sketch, "E21.7.0.19", {"start": v(-1.5, -1.45) * mm, "end": v(-1.5, 1.05) * mm});
            skLineSegment(sketch, "E21.7.0.20", {"start": v(-1.5, -1.45) * mm, "end": v(-3.75, -1.45) * mm});
            skLineSegment(sketch, "E21.7.0.21", {"start": v(-1.5, 6.05) * mm, "end": v(-3.75, 6.05) * mm});
            skPoint(sketch, "E21.7.0.22", {"position": v(-2.62, 4.8) * mm});
            skLineSegment(sketch, "E21.7.0.23", {"start": v(-1.5, 9.2) * mm, "end": v(-1.5, -1.45) * mm});
            skLineSegment(sketch, "E21.7.0.24", {"start": v(-1.5, 9.2) * mm, "end": v(-1.5, 6.2) * mm});
            skLineSegment(sketch, "E21.7.0.25", {"start": v(-3.75, 9.2) * mm, "end": v(-3.75, -1.45) * mm});
            skLineSegment(sketch, "E21.7.0.26", {"start": v(-3.75, 9.2) * mm, "end": v(-3.75, 6.2) * mm});
            skLineSegment(sketch, "E21.7.0.27", {"start": v(-1.5, 1.05) * mm, "end": v(-3.75, 1.05) * mm});
            skLineSegment(sketch, "E21.7.0.28", {"start": v(-1.5, 3.55) * mm, "end": v(-3.75, 3.55) * mm});
            skLineSegment(sketch, "E21.7.0.29", {"start": v(-3.75, 9.2) * mm, "end": v(-1.5, 9.2) * mm});
            skLineSegment(sketch, "E21.7.0.30", {"start": v(-2.33, 2) * mm, "end": v(-2.93, 2) * mm});
            skLineSegment(sketch, "E21.7.0.31", {"start": v(-2.93, 4.5) * mm, "end": v(-2.93, 5.1) * mm});
            skLineSegment(sketch, "E21.7.0.32", {"start": v(-2.33, 2.6) * mm, "end": v(-2.93, 2.6) * mm});
            skLineSegment(sketch, "E21.7.0.33", {"start": v(-2.33, -0.5) * mm, "end": v(-2.93, -0.5) * mm});
            skLineSegment(sketch, "E21.7.0.34", {"start": v(-2.33, 7.65) * mm, "end": v(-2.33, 8.25) * mm});
            skLineSegment(sketch, "E21.7.0.35", {"start": v(-2.33, 2) * mm, "end": v(-2.33, 2.6) * mm});
            skLineSegment(sketch, "E21.7.0.36", {"start": v(-2.93, -0.5) * mm, "end": v(-2.93, 0.1) * mm});
            skLineSegment(sketch, "E21.7.0.37", {"start": v(-2.33, -0.5) * mm, "end": v(-2.33, 0.1) * mm});
            skLineSegment(sketch, "E21.7.0.38", {"start": v(-2.33, 7.65) * mm, "end": v(-2.93, 7.65) * mm});
            skLineSegment(sketch, "E21.7.0.39", {"start": v(-2.93, 2) * mm, "end": v(-2.93, 2.6) * mm});
            skLineSegment(sketch, "E21.7.0.40", {"start": v(-2.93, 7.65) * mm, "end": v(-2.93, 8.25) * mm});
            skLineSegment(sketch, "E21.7.0.41", {"start": v(-2.33, 4.5) * mm, "end": v(-2.93, 4.5) * mm});
            skLineSegment(sketch, "E21.7.0.42", {"start": v(-2.33, 5.1) * mm, "end": v(-2.93, 5.1) * mm});
            skLineSegment(sketch, "E21.7.0.43", {"start": v(-2.33, 8.25) * mm, "end": v(-2.93, 8.25) * mm});
            skLineSegment(sketch, "E21.7.0.44", {"start": v(-2.33, 4.5) * mm, "end": v(-2.33, 5.1) * mm});
            skLineSegment(sketch, "E21.7.0.45", {"start": v(-2.33, 0.1) * mm, "end": v(-2.93, 0.1) * mm});
            skLineSegment(sketch, "E21.direction1", {"start": v(-21.95, -1.45) * mm, "end": v(-19.35, -1.45) * mm, "construction": true});
            skSolve(sketch);
        }
        {
            var Q0;
            {var subQ27=sQuery(id+"F2.wireOp",EDGE,"E2.top");Q0=makeQuery(id+"F2.imprint","IMPRINT",FACE,{"disambiguationData":[TD([[makeQuery(id+"F2.imprint","IMPRINT",EDGE,{"derivedFrom":subQ27}),1.0]])]});}
            var Q1;
            {var subQ27=sQuery(id+"F2.wireOp",EDGE,"E2.bottom");Q1=makeQuery(id+"F2.imprint","IMPRINT",FACE,{"disambiguationData":[TD([[makeQuery(id+"F2.imprint","IMPRINT",EDGE,{"derivedFrom":subQ27}),-1.0]])]});}
            var Q2;
            {var subQ1=sQuery(id+"F2.wireOp",EDGE,"E10.top");Q2=makeQuery(id+"F2.imprint","IMPRINT",FACE,{"disambiguationData":[TD([[makeQuery(id+"F2.imprint","IMPRINT",EDGE,{"derivedFrom":subQ1}),-1.0]])]});}
            var Q3;
            {var subQ10=sQuery(id+"F2.wireOp",EDGE,"E21.1.0.7");Q3=makeQuery(id+"F2.imprint","IMPRINT",FACE,{"disambiguationData":[TD([[makeQuery(id+"F2.imprint","IMPRINT",EDGE,{"derivedFrom":subQ10}),1.0]])]});}
            var Q4;
            {var subQ0=sQuery(id+"F2.wireOp",EDGE,"E21.7.0.33");Q4=makeQuery(id+"F2.imprint","IMPRINT",FACE,{"disambiguationData":[TD([[makeQuery(id+"F2.imprint","IMPRINT",EDGE,{"derivedFrom":subQ0}),1.0]])]});}
            var Q5;
            {var subQ0=sQuery(id+"F2.wireOp",EDGE,"E21.5.0.19");var subQ1=sQuery(id+"F2.wireOp",EDGE,"E6.top");var subQ2=makeQuery(id+"F2.imprint","INTERSECT",VERTEX,{"derivedFrom":[subQ1,subQ0]});Q5=makeQuery(id+"F2.imprint","IMPRINT",FACE,{"disambiguationData":[TD([[makeQuery(id+"F2.imprint","IMPRINT",EDGE,{"disambiguationData":[TD([[subQ2,1.0]])],"derivedFrom":subQ1}),-1.0]])]});}
            var Q6;
            {var subQ3=sQuery(id+"F0.wireOp",EDGE,"E0.left");var subQ4=makeQuery(id+"F1.opExtrude","CAP_EDGE",EDGE,{"disambiguationData":[OSD([subQ3])],"isStart":true});var subQ6=sQuery(id+"F2.wireOp",EDGE,"E21.6.0.19");var subQ9=makeQuery(id+"F2.imprint","INTERSECT",VERTEX,{"derivedFrom":[subQ4,subQ6]});Q6=makeQuery(id+"F2.imprint","IMPRINT",FACE,{"disambiguationData":[TD([[makeQuery(id+"F2.imprint","IMPRINT",EDGE,{"disambiguationData":[TD([[subQ9,1.0]])],"derivedFrom":subQ4}),-1.0]])]});}
            var Q7;
            {var subQ3=sQuery(id+"F0.wireOp",EDGE,"E0.left");var subQ4=makeQuery(id+"F1.opExtrude","CAP_EDGE",EDGE,{"disambiguationData":[OSD([subQ3])],"isStart":true});var subQ6=sQuery(id+"F2.wireOp",EDGE,"E21.2.0.19");var subQ9=makeQuery(id+"F2.imprint","INTERSECT",VERTEX,{"derivedFrom":[subQ4,subQ6]});Q7=makeQuery(id+"F2.imprint","IMPRINT",FACE,{"disambiguationData":[TD([[makeQuery(id+"F2.imprint","IMPRINT",EDGE,{"disambiguationData":[TD([[subQ9,1.0]])],"derivedFrom":subQ4}),-1.0]])]});}
            var Q8;
            {var subQ1=sQuery(id+"F2.wireOp",EDGE,"E21.4.0.8");Q8=makeQuery(id+"F2.imprint","IMPRINT",FACE,{"disambiguationData":[TD([[makeQuery(id+"F2.imprint","IMPRINT",EDGE,{"derivedFrom":subQ1}),-1.0]])]});}
            var Q9;
            {var subQ0=sQuery(id+"F2.wireOp",EDGE,"E21.6.0.19");var subQ1=sQuery(id+"F2.wireOp",EDGE,"E6.top");var subQ2=makeQuery(id+"F2.imprint","INTERSECT",VERTEX,{"derivedFrom":[subQ1,subQ0]});Q9=makeQuery(id+"F2.imprint","IMPRINT",FACE,{"disambiguationData":[TD([[makeQuery(id+"F2.imprint","IMPRINT",EDGE,{"disambiguationData":[TD([[subQ2,1.0]])],"derivedFrom":subQ1}),-1.0]])]});}
            var Q10;
            {var subQ6=sQuery(id+"F2.wireOp",EDGE,"E21.4.0.8");Q10=makeQuery(id+"F2.imprint","IMPRINT",FACE,{"disambiguationData":[TD([[makeQuery(id+"F2.imprint","IMPRINT",EDGE,{"derivedFrom":subQ6}),1.0]])]});}
            var Q11;
            {var subQ1=sQuery(id+"F2.wireOp",EDGE,"E21.5.0.0");Q11=makeQuery(id+"F2.imprint","IMPRINT",FACE,{"disambiguationData":[TD([[makeQuery(id+"F2.imprint","IMPRINT",EDGE,{"derivedFrom":subQ1}),-1.0]])]});}
            var Q12;
            {var subQ1=sQuery(id+"F2.wireOp",EDGE,"E9.top");Q12=makeQuery(id+"F2.imprint","IMPRINT",FACE,{"disambiguationData":[TD([[makeQuery(id+"F2.imprint","IMPRINT",EDGE,{"derivedFrom":subQ1}),-1.0]])]});}
            var Q13;
            {var subQ1=sQuery(id+"F2.wireOp",EDGE,"E21.1.0.0");Q13=makeQuery(id+"F2.imprint","IMPRINT",FACE,{"disambiguationData":[TD([[makeQuery(id+"F2.imprint","IMPRINT",EDGE,{"derivedFrom":subQ1}),-1.0]])]});}
            var Q14;
            {var subQ1=sQuery(id+"F2.wireOp",EDGE,"E21.6.0.8");Q14=makeQuery(id+"F2.imprint","IMPRINT",FACE,{"disambiguationData":[TD([[makeQuery(id+"F2.imprint","IMPRINT",EDGE,{"derivedFrom":subQ1}),-1.0]])]});}
            var Q15;
            {var subQ0=sQuery(id+"F2.wireOp",EDGE,"E21.3.0.33");Q15=makeQuery(id+"F2.imprint","IMPRINT",FACE,{"disambiguationData":[TD([[makeQuery(id+"F2.imprint","IMPRINT",EDGE,{"derivedFrom":subQ0}),1.0]])]});}
            var Q16;
            {var subQ11=sQuery(id+"F2.wireOp",EDGE,"E21.2.0.0");Q16=makeQuery(id+"F2.imprint","IMPRINT",FACE,{"disambiguationData":[TD([[makeQuery(id+"F2.imprint","IMPRINT",EDGE,{"derivedFrom":subQ11}),1.0]])]});}
            var Q17;
            {var subQ5=sQuery(id+"F2.wireOp",EDGE,"E21.5.0.8");Q17=makeQuery(id+"F2.imprint","IMPRINT",FACE,{"disambiguationData":[TD([[makeQuery(id+"F2.imprint","IMPRINT",EDGE,{"derivedFrom":subQ5}),1.0]])]});}
            var Q18;
            {var subQ5=sQuery(id+"F2.wireOp",EDGE,"E21.2.0.5");Q18=makeQuery(id+"F2.imprint","IMPRINT",FACE,{"disambiguationData":[TD([[makeQuery(id+"F2.imprint","IMPRINT",EDGE,{"derivedFrom":subQ5}),1.0]])]});}
            var Q19;
            {var subQ1=sQuery(id+"F2.wireOp",EDGE,"E9.top");Q19=makeQuery(id+"F2.imprint","IMPRINT",FACE,{"disambiguationData":[TD([[makeQuery(id+"F2.imprint","IMPRINT",EDGE,{"derivedFrom":subQ1}),1.0]])]});}
            var Q20;
            Q20=makeQuery(id+"F2.imprint","IMPRINT",FACE,{"disambiguationData":[TD([[makeQuery(id+"F2.imprint","IMPRINT",EDGE,{"derivedFrom":sQuery(id+"F2.wireOp",EDGE,"E21.1.0.5")}),-1.0]])]});
            var Q21;
            {var subQ8=sQuery(id+"F2.wireOp",EDGE,"E21.6.0.0");Q21=makeQuery(id+"F2.imprint","IMPRINT",FACE,{"disambiguationData":[TD([[makeQuery(id+"F2.imprint","IMPRINT",EDGE,{"derivedFrom":subQ8}),1.0]])]});}
            var Q22;
            {var subQ0=sQuery(id+"F2.wireOp",EDGE,"E21.2.0.19");var subQ1=sQuery(id+"F2.wireOp",EDGE,"E6.top");var subQ2=makeQuery(id+"F2.imprint","INTERSECT",VERTEX,{"derivedFrom":[subQ1,subQ0]});Q22=makeQuery(id+"F2.imprint","IMPRINT",FACE,{"disambiguationData":[TD([[makeQuery(id+"F2.imprint","IMPRINT",EDGE,{"disambiguationData":[TD([[subQ2,1.0]])],"derivedFrom":subQ1}),-1.0]])]});}
            var Q23;
            {var subQ5=sQuery(id+"F2.wireOp",EDGE,"E21.2.0.8");Q23=makeQuery(id+"F2.imprint","IMPRINT",FACE,{"disambiguationData":[TD([[makeQuery(id+"F2.imprint","IMPRINT",EDGE,{"derivedFrom":subQ5}),1.0]])]});}
            var Q24;
            {var subQ1=sQuery(id+"F2.wireOp",EDGE,"E21.4.0.5");Q24=makeQuery(id+"F2.imprint","IMPRINT",FACE,{"disambiguationData":[TD([[makeQuery(id+"F2.imprint","IMPRINT",EDGE,{"derivedFrom":subQ1}),1.0]])]});}
            var Q25;
            {var subQ0=sQuery(id+"F2.wireOp",EDGE,"E21.7.0.0");Q25=makeQuery(id+"F2.imprint","IMPRINT",FACE,{"disambiguationData":[TD([[makeQuery(id+"F2.imprint","IMPRINT",EDGE,{"derivedFrom":subQ0}),-1.0]])]});}
            var Q26;
            {var subQ1=sQuery(id+"F2.wireOp",EDGE,"E21.3.0.5");Q26=makeQuery(id+"F2.imprint","IMPRINT",FACE,{"disambiguationData":[TD([[makeQuery(id+"F2.imprint","IMPRINT",EDGE,{"derivedFrom":subQ1}),1.0]])]});}
            var Q27;
            {var subQ1=sQuery(id+"F2.wireOp",EDGE,"E21.6.0.0");Q27=makeQuery(id+"F2.imprint","IMPRINT",FACE,{"disambiguationData":[TD([[makeQuery(id+"F2.imprint","IMPRINT",EDGE,{"derivedFrom":subQ1}),-1.0]])]});}
            var Q28;
            {var subQ3=sQuery(id+"F0.wireOp",EDGE,"E0.left");var subQ4=makeQuery(id+"F1.opExtrude","CAP_EDGE",EDGE,{"disambiguationData":[OSD([subQ3])],"isStart":true});var subQ6=sQuery(id+"F2.wireOp",EDGE,"E21.1.0.19");var subQ9=makeQuery(id+"F2.imprint","INTERSECT",VERTEX,{"derivedFrom":[subQ4,subQ6]});Q28=makeQuery(id+"F2.imprint","IMPRINT",FACE,{"disambiguationData":[TD([[makeQuery(id+"F2.imprint","IMPRINT",EDGE,{"disambiguationData":[TD([[subQ9,1.0]])],"derivedFrom":subQ4}),-1.0]])]});}
            var Q29;
            {var subQ1=sQuery(id+"F2.wireOp",EDGE,"E21.3.0.0");Q29=makeQuery(id+"F2.imprint","IMPRINT",FACE,{"disambiguationData":[TD([[makeQuery(id+"F2.imprint","IMPRINT",EDGE,{"derivedFrom":subQ1}),-1.0]])]});}
            var Q30;
            Q30=makeQuery(id+"F2.imprint","IMPRINT",FACE,{"disambiguationData":[TD([[makeQuery(id+"F2.imprint","IMPRINT",EDGE,{"derivedFrom":sQuery(id+"F2.wireOp",EDGE,"E21.7.0.5")}),-1.0]])]});
            var Q31;
            {var subQ1=sQuery(id+"F2.wireOp",EDGE,"E21.1.0.5");Q31=makeQuery(id+"F2.imprint","IMPRINT",FACE,{"disambiguationData":[TD([[makeQuery(id+"F2.imprint","IMPRINT",EDGE,{"derivedFrom":subQ1}),1.0]])]});}
            var Q32;
            {var subQ1=sQuery(id+"F2.wireOp",EDGE,"E21.5.0.8");Q32=makeQuery(id+"F2.imprint","IMPRINT",FACE,{"disambiguationData":[TD([[makeQuery(id+"F2.imprint","IMPRINT",EDGE,{"derivedFrom":subQ1}),-1.0]])]});}
            var Q33;
            {var subQ0=sQuery(id+"F2.wireOp",EDGE,"E21.4.0.0");Q33=makeQuery(id+"F2.imprint","IMPRINT",FACE,{"disambiguationData":[TD([[makeQuery(id+"F2.imprint","IMPRINT",EDGE,{"derivedFrom":subQ0}),-1.0]])]});}
            var Q34;
            {var subQ11=sQuery(id+"F2.wireOp",EDGE,"E21.5.0.0");Q34=makeQuery(id+"F2.imprint","IMPRINT",FACE,{"disambiguationData":[TD([[makeQuery(id+"F2.imprint","IMPRINT",EDGE,{"derivedFrom":subQ11}),1.0]])]});}
            var Q35;
            {var subQ1=sQuery(id+"F2.wireOp",EDGE,"E21.1.0.8");Q35=makeQuery(id+"F2.imprint","IMPRINT",FACE,{"disambiguationData":[TD([[makeQuery(id+"F2.imprint","IMPRINT",EDGE,{"derivedFrom":subQ1}),-1.0]])]});}
            var Q36;
            {var subQ0=sQuery(id+"F2.wireOp",EDGE,"E21.4.0.19");var subQ1=sQuery(id+"F2.wireOp",EDGE,"E6.top");var subQ2=makeQuery(id+"F2.imprint","INTERSECT",VERTEX,{"derivedFrom":[subQ1,subQ0]});Q36=makeQuery(id+"F2.imprint","IMPRINT",FACE,{"disambiguationData":[TD([[makeQuery(id+"F2.imprint","IMPRINT",EDGE,{"disambiguationData":[TD([[subQ2,1.0]])],"derivedFrom":subQ1}),-1.0]])]});}
            var Q37;
            {var subQ9=sQuery(id+"F2.wireOp",EDGE,"E21.4.0.0");Q37=makeQuery(id+"F2.imprint","IMPRINT",FACE,{"disambiguationData":[TD([[makeQuery(id+"F2.imprint","IMPRINT",EDGE,{"derivedFrom":subQ9}),1.0]])]});}
            var Q38;
            {var subQ1=sQuery(id+"F2.wireOp",EDGE,"E21.2.0.0");Q38=makeQuery(id+"F2.imprint","IMPRINT",FACE,{"disambiguationData":[TD([[makeQuery(id+"F2.imprint","IMPRINT",EDGE,{"derivedFrom":subQ1}),-1.0]])]});}
            var Q39;
            {var subQ5=sQuery(id+"F2.wireOp",EDGE,"E21.3.0.8");Q39=makeQuery(id+"F2.imprint","IMPRINT",FACE,{"disambiguationData":[TD([[makeQuery(id+"F2.imprint","IMPRINT",EDGE,{"derivedFrom":subQ5}),1.0]])]});}
            var Q40;
            Q40=makeQuery(id+"F2.imprint","IMPRINT",FACE,{"disambiguationData":[TD([[makeQuery(id+"F2.imprint","IMPRINT",EDGE,{"derivedFrom":sQuery(id+"F2.wireOp",EDGE,"E21.6.0.5")}),-1.0]])]});
            var Q41;
            {var subQ0=sQuery(id+"F2.wireOp",EDGE,"E21.2.0.33");Q41=makeQuery(id+"F2.imprint","IMPRINT",FACE,{"disambiguationData":[TD([[makeQuery(id+"F2.imprint","IMPRINT",EDGE,{"derivedFrom":subQ0}),1.0]])]});}
            var Q42;
            {var subQ0=sQuery(id+"F2.wireOp",EDGE,"E10.top");Q42=makeQuery(id+"F2.imprint","IMPRINT",FACE,{"disambiguationData":[TD([[makeQuery(id+"F2.imprint","IMPRINT",EDGE,{"derivedFrom":subQ0}),1.0]])]});}
            var Q43;
            {var subQ1=sQuery(id+"F2.wireOp",EDGE,"E21.2.0.8");Q43=makeQuery(id+"F2.imprint","IMPRINT",FACE,{"disambiguationData":[TD([[makeQuery(id+"F2.imprint","IMPRINT",EDGE,{"derivedFrom":subQ1}),-1.0]])]});}
            var Q44;
            {var subQ0=sQuery(id+"F2.wireOp",EDGE,"E19.bottom");Q44=makeQuery(id+"F2.imprint","IMPRINT",FACE,{"disambiguationData":[TD([[makeQuery(id+"F2.imprint","IMPRINT",EDGE,{"derivedFrom":subQ0}),1.0]])]});}
            var Q45;
            {var subQ0=sQuery(id+"F2.wireOp",EDGE,"E21.6.0.33");Q45=makeQuery(id+"F2.imprint","IMPRINT",FACE,{"disambiguationData":[TD([[makeQuery(id+"F2.imprint","IMPRINT",EDGE,{"derivedFrom":subQ0}),1.0]])]});}
            var Q46;
            {var subQ0=sQuery(id+"F2.wireOp",EDGE,"E21.1.0.33");Q46=makeQuery(id+"F2.imprint","IMPRINT",FACE,{"disambiguationData":[TD([[makeQuery(id+"F2.imprint","IMPRINT",EDGE,{"derivedFrom":subQ0}),1.0]])]});}
            var Q47;
            Q47=makeQuery(id+"F2.imprint","IMPRINT",FACE,{"disambiguationData":[TD([[makeQuery(id+"F2.imprint","IMPRINT",EDGE,{"derivedFrom":sQuery(id+"F2.wireOp",EDGE,"E21.3.0.5")}),-1.0]])]});
            var Q48;
            {var subQ4=sQuery(id+"F2.wireOp",EDGE,"E21.1.0.0");Q48=makeQuery(id+"F2.imprint","IMPRINT",FACE,{"disambiguationData":[TD([[makeQuery(id+"F2.imprint","IMPRINT",EDGE,{"derivedFrom":subQ4}),1.0]])]});}
            var Q49;
            {var subQ0=sQuery(id+"F2.wireOp",EDGE,"E2.right");var subQ1=sQuery(id+"F0.wireOp",EDGE,"E0.left");var subQ2=makeQuery(id+"F1.opExtrude","CAP_EDGE",EDGE,{"disambiguationData":[OSD([subQ1])],"isStart":true});var subQ3=makeQuery(id+"F2.imprint","INTERSECT",VERTEX,{"derivedFrom":[subQ2,subQ0]});var subQ7=makeQuery(id+"F1.opExtrude","CAP_EDGE",EDGE,{"disambiguationData":[OSD([subQ1])],"isStart":false});var subQ9=makeQuery(id+"F2.imprint","INTERSECT",VERTEX,{"derivedFrom":[subQ7,subQ0]});Q49=makeQuery(id+"F2.imprint","IMPRINT",FACE,{"disambiguationData":[TD([[makeQuery(id+"F2.imprint","IMPRINT",EDGE,{"disambiguationData":[TD([[subQ3,1.0],[subQ9,-1.0]])],"derivedFrom":subQ0}),1.0]])]});}
            var Q50;
            Q50=makeQuery(id+"F1.opExtrude","SWEPT_FACE",FACE,{"disambiguationData":[OSD([sQuery(id+"F0.wireOp",EDGE,"E0.left")])]});
            var Q51;
            {var subQ0=sQuery(id+"F2.wireOp",EDGE,"E21.3.0.9");Q51=makeQuery(id+"F2.imprint","IMPRINT",FACE,{"disambiguationData":[TD([[makeQuery(id+"F2.imprint","IMPRINT",EDGE,{"derivedFrom":subQ0}),1.0]])]});}
            var Q52;
            {var subQ0=sQuery(id+"F2.wireOp",EDGE,"E21.2.0.9");Q52=makeQuery(id+"F2.imprint","IMPRINT",FACE,{"disambiguationData":[TD([[makeQuery(id+"F2.imprint","IMPRINT",EDGE,{"derivedFrom":subQ0}),1.0]])]});}
            var Q53;
            {var subQ0=sQuery(id+"F2.wireOp",EDGE,"E21.4.0.33");Q53=makeQuery(id+"F2.imprint","IMPRINT",FACE,{"disambiguationData":[TD([[makeQuery(id+"F2.imprint","IMPRINT",EDGE,{"derivedFrom":subQ0}),1.0]])]});}
            var Q54;
            {var subQ1=sQuery(id+"F2.wireOp",EDGE,"E21.6.0.5");Q54=makeQuery(id+"F2.imprint","IMPRINT",FACE,{"disambiguationData":[TD([[makeQuery(id+"F2.imprint","IMPRINT",EDGE,{"derivedFrom":subQ1}),1.0]])]});}
            var Q55;
            {var subQ0=sQuery(id+"F2.wireOp",EDGE,"E8.top");Q55=makeQuery(id+"F2.imprint","IMPRINT",FACE,{"disambiguationData":[TD([[makeQuery(id+"F2.imprint","IMPRINT",EDGE,{"derivedFrom":subQ0}),1.0]])]});}
            var Q56;
            {var subQ0=sQuery(id+"F2.wireOp",EDGE,"E21.1.0.9");Q56=makeQuery(id+"F2.imprint","IMPRINT",FACE,{"disambiguationData":[TD([[makeQuery(id+"F2.imprint","IMPRINT",EDGE,{"derivedFrom":subQ0}),1.0]])]});}
            var Q57;
            {var subQ0=sQuery(id+"F2.wireOp",EDGE,"E21.4.0.9");Q57=makeQuery(id+"F2.imprint","IMPRINT",FACE,{"disambiguationData":[TD([[makeQuery(id+"F2.imprint","IMPRINT",EDGE,{"derivedFrom":subQ0}),1.0]])]});}
            var Q58;
            {var subQ0=sQuery(id+"F2.wireOp",EDGE,"E21.7.0.9");Q58=makeQuery(id+"F2.imprint","IMPRINT",FACE,{"disambiguationData":[TD([[makeQuery(id+"F2.imprint","IMPRINT",EDGE,{"derivedFrom":subQ0}),1.0]])]});}
            var Q59;
            {var subQ1=sQuery(id+"F2.wireOp",EDGE,"E21.5.0.5");Q59=makeQuery(id+"F2.imprint","IMPRINT",FACE,{"disambiguationData":[TD([[makeQuery(id+"F2.imprint","IMPRINT",EDGE,{"derivedFrom":subQ1}),1.0]])]});}
            var Q60;
            {var subQ3=sQuery(id+"F0.wireOp",EDGE,"E0.left");var subQ4=makeQuery(id+"F1.opExtrude","CAP_EDGE",EDGE,{"disambiguationData":[OSD([subQ3])],"isStart":true});var subQ6=sQuery(id+"F2.wireOp",EDGE,"E21.3.0.19");var subQ9=makeQuery(id+"F2.imprint","INTERSECT",VERTEX,{"derivedFrom":[subQ4,subQ6]});Q60=makeQuery(id+"F2.imprint","IMPRINT",FACE,{"disambiguationData":[TD([[makeQuery(id+"F2.imprint","IMPRINT",EDGE,{"disambiguationData":[TD([[subQ9,1.0]])],"derivedFrom":subQ4}),-1.0]])]});}
            var Q61;
            {var subQ3=sQuery(id+"F0.wireOp",EDGE,"E0.left");var subQ4=makeQuery(id+"F1.opExtrude","CAP_EDGE",EDGE,{"disambiguationData":[OSD([subQ3])],"isStart":true});var subQ6=sQuery(id+"F2.wireOp",EDGE,"E21.5.0.19");var subQ7=makeQuery(id+"F2.imprint","INTERSECT",VERTEX,{"derivedFrom":[subQ4,subQ6]});Q61=makeQuery(id+"F2.imprint","IMPRINT",FACE,{"disambiguationData":[TD([[makeQuery(id+"F2.imprint","IMPRINT",EDGE,{"disambiguationData":[TD([[subQ7,1.0]])],"derivedFrom":subQ4}),-1.0]])]});}
            var Q62;
            {var subQ0=sQuery(id+"F2.wireOp",EDGE,"E21.5.0.33");Q62=makeQuery(id+"F2.imprint","IMPRINT",FACE,{"disambiguationData":[TD([[makeQuery(id+"F2.imprint","IMPRINT",EDGE,{"derivedFrom":subQ0}),1.0]])]});}
            var Q63;
            {var subQ3=sQuery(id+"F2.wireOp",EDGE,"E12.top");Q63=makeQuery(id+"F2.imprint","IMPRINT",FACE,{"disambiguationData":[TD([[makeQuery(id+"F2.imprint","IMPRINT",EDGE,{"derivedFrom":subQ3}),1.0]])]});}
            var Q64;
            {var subQ11=sQuery(id+"F2.wireOp",EDGE,"E21.3.0.0");Q64=makeQuery(id+"F2.imprint","IMPRINT",FACE,{"disambiguationData":[TD([[makeQuery(id+"F2.imprint","IMPRINT",EDGE,{"derivedFrom":subQ11}),1.0]])]});}
            var Q65;
            {var subQ1=sQuery(id+"F2.wireOp",EDGE,"E21.7.0.8");Q65=makeQuery(id+"F2.imprint","IMPRINT",FACE,{"disambiguationData":[TD([[makeQuery(id+"F2.imprint","IMPRINT",EDGE,{"derivedFrom":subQ1}),-1.0]])]});}
            var Q66;
            {var subQ0=sQuery(id+"F2.wireOp",EDGE,"E21.5.0.9");Q66=makeQuery(id+"F2.imprint","IMPRINT",FACE,{"disambiguationData":[TD([[makeQuery(id+"F2.imprint","IMPRINT",EDGE,{"derivedFrom":subQ0}),1.0]])]});}
            var Q67;
            Q67=makeQuery(id+"F2.imprint","IMPRINT",FACE,{"disambiguationData":[TD([[makeQuery(id+"F2.imprint","IMPRINT",EDGE,{"derivedFrom":sQuery(id+"F2.wireOp",EDGE,"E21.2.0.5")}),-1.0]])]});
            var Q68;
            {var subQ0=sQuery(id+"F2.wireOp",EDGE,"E21.3.0.19");var subQ1=sQuery(id+"F2.wireOp",EDGE,"E6.top");var subQ2=makeQuery(id+"F2.imprint","INTERSECT",VERTEX,{"derivedFrom":[subQ1,subQ0]});Q68=makeQuery(id+"F2.imprint","IMPRINT",FACE,{"disambiguationData":[TD([[makeQuery(id+"F2.imprint","IMPRINT",EDGE,{"disambiguationData":[TD([[subQ2,1.0]])],"derivedFrom":subQ1}),-1.0]])]});}
            var Q69;
            {var subQ0=sQuery(id+"F2.wireOp",EDGE,"E21.6.0.9");Q69=makeQuery(id+"F2.imprint","IMPRINT",FACE,{"disambiguationData":[TD([[makeQuery(id+"F2.imprint","IMPRINT",EDGE,{"derivedFrom":subQ0}),1.0]])]});}
            var Q70;
            {var subQ0=sQuery(id+"F2.wireOp",EDGE,"E21.1.0.19");var subQ1=sQuery(id+"F2.wireOp",EDGE,"E6.top");var subQ2=makeQuery(id+"F2.imprint","INTERSECT",VERTEX,{"derivedFrom":[subQ1,subQ0]});Q70=makeQuery(id+"F2.imprint","IMPRINT",FACE,{"disambiguationData":[TD([[makeQuery(id+"F2.imprint","IMPRINT",EDGE,{"disambiguationData":[TD([[subQ2,1.0]])],"derivedFrom":subQ1}),-1.0]])]});}
            var Q71;
            {var subQ5=sQuery(id+"F2.wireOp",EDGE,"E21.1.0.8");Q71=makeQuery(id+"F2.imprint","IMPRINT",FACE,{"disambiguationData":[TD([[makeQuery(id+"F2.imprint","IMPRINT",EDGE,{"derivedFrom":subQ5}),1.0]])]});}
            var Q72;
            Q72=makeQuery(id+"F2.imprint","IMPRINT",FACE,{"disambiguationData":[TD([[makeQuery(id+"F2.imprint","IMPRINT",EDGE,{"derivedFrom":sQuery(id+"F2.wireOp",EDGE,"E21.4.0.5")}),-1.0]])]});
            var Q73;
            Q73=makeQuery(id+"F2.imprint","IMPRINT",FACE,{"disambiguationData":[TD([[makeQuery(id+"F2.imprint","IMPRINT",EDGE,{"derivedFrom":sQuery(id+"F2.wireOp",EDGE,"E21.5.0.5")}),-1.0]])]});
            var Q74;
            {var subQ1=sQuery(id+"F2.wireOp",EDGE,"E21.7.0.5");Q74=makeQuery(id+"F2.imprint","IMPRINT",FACE,{"disambiguationData":[TD([[makeQuery(id+"F2.imprint","IMPRINT",EDGE,{"derivedFrom":subQ1}),1.0]])]});}
            var Q75;
            {var subQ0=sQuery(id+"F2.wireOp",EDGE,"E2.left");var subQ1=sQuery(id+"F0.wireOp",EDGE,"E0.left");var subQ2=makeQuery(id+"F1.opExtrude","CAP_EDGE",EDGE,{"disambiguationData":[OSD([subQ1])],"isStart":true});var subQ3=makeQuery(id+"F2.imprint","INTERSECT",VERTEX,{"derivedFrom":[subQ2,subQ0]});var subQ4=makeQuery(id+"F1.opExtrude","CAP_EDGE",EDGE,{"disambiguationData":[OSD([subQ1])],"isStart":false});var subQ5=makeQuery(id+"F2.imprint","INTERSECT",VERTEX,{"derivedFrom":[subQ4,subQ0]});Q75=makeQuery(id+"F2.imprint","IMPRINT",FACE,{"disambiguationData":[TD([[makeQuery(id+"F2.imprint","IMPRINT",EDGE,{"disambiguationData":[TD([[subQ3,1.0],[subQ5,-1.0]])],"derivedFrom":subQ0}),-1.0]])]});}
            var Q76;
            {var subQ0=sQuery(id+"F2.wireOp",EDGE,"E7");var subQ1=sQuery(id+"F2.wireOp",EDGE,"E6.top");var subQ2=makeQuery(id+"F2.imprint","INTERSECT",VERTEX,{"derivedFrom":[subQ1,subQ0]});Q76=makeQuery(id+"F2.imprint","IMPRINT",FACE,{"disambiguationData":[TD([[makeQuery(id+"F2.imprint","IMPRINT",EDGE,{"disambiguationData":[TD([[subQ2,1.0]])],"derivedFrom":subQ1}),-1.0]])]});}
            var Q77;
            {var subQ0=sQuery(id+"F2.wireOp",EDGE,"E21.7.0.19");var subQ1=sQuery(id+"F2.wireOp",EDGE,"E6.top");var subQ2=makeQuery(id+"F2.imprint","INTERSECT",VERTEX,{"derivedFrom":[subQ1,subQ0]});Q77=makeQuery(id+"F2.imprint","IMPRINT",FACE,{"disambiguationData":[TD([[makeQuery(id+"F2.imprint","IMPRINT",EDGE,{"disambiguationData":[TD([[subQ2,1.0]])],"derivedFrom":subQ1}),-1.0]])]});}
            var Q78;
            {var subQ5=sQuery(id+"F2.wireOp",EDGE,"E21.7.0.8");Q78=makeQuery(id+"F2.imprint","IMPRINT",FACE,{"disambiguationData":[TD([[makeQuery(id+"F2.imprint","IMPRINT",EDGE,{"derivedFrom":subQ5}),1.0]])]});}
            var Q79;
            {var subQ5=sQuery(id+"F2.wireOp",EDGE,"E21.6.0.8");Q79=makeQuery(id+"F2.imprint","IMPRINT",FACE,{"disambiguationData":[TD([[makeQuery(id+"F2.imprint","IMPRINT",EDGE,{"derivedFrom":subQ5}),1.0]])]});}
            var Q80;
            {var subQ3=sQuery(id+"F0.wireOp",EDGE,"E0.left");var subQ4=makeQuery(id+"F1.opExtrude","CAP_EDGE",EDGE,{"disambiguationData":[OSD([subQ3])],"isStart":true});var subQ6=sQuery(id+"F2.wireOp",EDGE,"E21.4.0.19");var subQ9=makeQuery(id+"F2.imprint","INTERSECT",VERTEX,{"derivedFrom":[subQ4,subQ6]});Q80=makeQuery(id+"F2.imprint","IMPRINT",FACE,{"disambiguationData":[TD([[makeQuery(id+"F2.imprint","IMPRINT",EDGE,{"disambiguationData":[TD([[subQ9,1.0]])],"derivedFrom":subQ4}),-1.0]])]});}
            var Q81;
            {var subQ1=sQuery(id+"F2.wireOp",EDGE,"E21.3.0.8");Q81=makeQuery(id+"F2.imprint","IMPRINT",FACE,{"disambiguationData":[TD([[makeQuery(id+"F2.imprint","IMPRINT",EDGE,{"derivedFrom":subQ1}),-1.0]])]});}
            var Q82;
            {var subQ0=sQuery(id+"F2.wireOp",EDGE,"E21.2.0.9");Q82=makeQuery(id+"F2.imprint","IMPRINT",FACE,{"disambiguationData":[TD([[makeQuery(id+"F2.imprint","IMPRINT",EDGE,{"derivedFrom":subQ0}),-1.0]])]});}
            var Q83;
            {var subQ0=sQuery(id+"F2.wireOp",EDGE,"E21.5.0.9");Q83=makeQuery(id+"F2.imprint","IMPRINT",FACE,{"disambiguationData":[TD([[makeQuery(id+"F2.imprint","IMPRINT",EDGE,{"derivedFrom":subQ0}),-1.0]])]});}
            var Q84;
            {var subQ0=sQuery(id+"F2.wireOp",EDGE,"E8.top");Q84=makeQuery(id+"F2.imprint","IMPRINT",FACE,{"disambiguationData":[TD([[makeQuery(id+"F2.imprint","IMPRINT",EDGE,{"derivedFrom":subQ0}),-1.0]])]});}
            var Q85;
            {var subQ0=sQuery(id+"F2.wireOp",EDGE,"E21.1.0.9");Q85=makeQuery(id+"F2.imprint","IMPRINT",FACE,{"disambiguationData":[TD([[makeQuery(id+"F2.imprint","IMPRINT",EDGE,{"derivedFrom":subQ0}),-1.0]])]});}
            var Q86;
            {var subQ0=sQuery(id+"F2.wireOp",EDGE,"E6.left");var subQ1=sQuery(id+"F0.wireOp",EDGE,"E0.left");var subQ8=makeQuery(id+"F1.opExtrude","CAP_EDGE",EDGE,{"disambiguationData":[OSD([subQ1])],"isStart":false});var subQ10=makeQuery(id+"F2.imprint","INTERSECT",VERTEX,{"derivedFrom":[subQ8,subQ0]});Q86=makeQuery(id+"F2.imprint","IMPRINT",FACE,{"disambiguationData":[TD([[makeQuery(id+"F2.imprint","IMPRINT",EDGE,{"disambiguationData":[TD([[subQ10,-1.0]])],"derivedFrom":subQ0}),-1.0]])]});}
            var Q87;
            {var subQ0=sQuery(id+"F2.wireOp",EDGE,"E21.7.0.0");Q87=makeQuery(id+"F2.imprint","IMPRINT",FACE,{"disambiguationData":[TD([[makeQuery(id+"F2.imprint","IMPRINT",EDGE,{"derivedFrom":subQ0}),1.0]])]});}
            var Q88;
            {var subQ0=sQuery(id+"F2.wireOp",EDGE,"E21.6.0.9");Q88=makeQuery(id+"F2.imprint","IMPRINT",FACE,{"disambiguationData":[TD([[makeQuery(id+"F2.imprint","IMPRINT",EDGE,{"derivedFrom":subQ0}),-1.0]])]});}
            var Q89;
            {var subQ8=sQuery(id+"F2.wireOp",EDGE,"E7");var subQ9=makeQuery(id+"F2.imprint","INTERSECT",VERTEX,{"derivedFrom":[subQ8,sQuery(id+"F2.wireOp",EDGE,"E9.top")]});Q89=makeQuery(id+"F2.imprint","IMPRINT",FACE,{"disambiguationData":[TD([[makeQuery(id+"F2.imprint","IMPRINT",EDGE,{"disambiguationData":[TD([[subQ9,-1.0]])],"derivedFrom":subQ8}),1.0]])]});}
            var Q90;
            {var subQ0=sQuery(id+"F2.wireOp",EDGE,"E21.3.0.9");Q90=makeQuery(id+"F2.imprint","IMPRINT",FACE,{"disambiguationData":[TD([[makeQuery(id+"F2.imprint","IMPRINT",EDGE,{"derivedFrom":subQ0}),-1.0]])]});}
            var Q91;
            {var subQ0=sQuery(id+"F2.wireOp",EDGE,"E21.3.0.45");Q91=makeQuery(id+"F2.imprint","IMPRINT",FACE,{"disambiguationData":[TD([[makeQuery(id+"F2.imprint","IMPRINT",EDGE,{"derivedFrom":subQ0}),1.0]])]});}
            var Q92;
            Q92=makeQuery(id+"F2.imprint","IMPRINT",FACE,{"disambiguationData":[TD([[makeQuery(id+"F2.imprint","IMPRINT",EDGE,{"derivedFrom":sQuery(id+"F2.wireOp",EDGE,"E21.4.0.30")}),-1.0]])]});
            var Q93;
            {var subQ0=sQuery(id+"F2.wireOp",EDGE,"E21.5.0.33");Q93=makeQuery(id+"F2.imprint","IMPRINT",FACE,{"disambiguationData":[TD([[makeQuery(id+"F2.imprint","IMPRINT",EDGE,{"derivedFrom":subQ0}),-1.0]])]});}
            var Q94;
            {var subQ0=sQuery(id+"F2.wireOp",EDGE,"E21.7.0.9");Q94=makeQuery(id+"F2.imprint","IMPRINT",FACE,{"disambiguationData":[TD([[makeQuery(id+"F2.imprint","IMPRINT",EDGE,{"derivedFrom":subQ0}),-1.0]])]});}
            var Q95;
            {var subQ0=sQuery(id+"F2.wireOp",EDGE,"E21.6.0.33");Q95=makeQuery(id+"F2.imprint","IMPRINT",FACE,{"disambiguationData":[TD([[makeQuery(id+"F2.imprint","IMPRINT",EDGE,{"derivedFrom":subQ0}),-1.0]])]});}
            var Q96;
            Q96=makeQuery(id+"F2.imprint","IMPRINT",FACE,{"disambiguationData":[TD([[makeQuery(id+"F2.imprint","IMPRINT",EDGE,{"derivedFrom":sQuery(id+"F2.wireOp",EDGE,"E21.7.0.31")}),-1.0]])]});
            var Q97;
            {var subQ0=sQuery(id+"F2.wireOp",EDGE,"E21.5.0.45");Q97=makeQuery(id+"F2.imprint","IMPRINT",FACE,{"disambiguationData":[TD([[makeQuery(id+"F2.imprint","IMPRINT",EDGE,{"derivedFrom":subQ0}),1.0]])]});}
            var Q98;
            Q98=makeQuery(id+"F2.imprint","IMPRINT",FACE,{"disambiguationData":[TD([[makeQuery(id+"F2.imprint","IMPRINT",EDGE,{"derivedFrom":sQuery(id+"F2.wireOp",EDGE,"E21.1.0.30")}),-1.0]])]});
            var Q99;
            Q99=makeQuery(id+"F2.imprint","IMPRINT",FACE,{"disambiguationData":[TD([[makeQuery(id+"F2.imprint","IMPRINT",EDGE,{"derivedFrom":sQuery(id+"F2.wireOp",EDGE,"E21.2.0.31")}),-1.0]])]});
            var Q100;
            {var subQ0=sQuery(id+"F2.wireOp",EDGE,"E21.1.0.45");Q100=makeQuery(id+"F2.imprint","IMPRINT",FACE,{"disambiguationData":[TD([[makeQuery(id+"F2.imprint","IMPRINT",EDGE,{"derivedFrom":subQ0}),1.0]])]});}
            var Q101;
            Q101=makeQuery(id+"F2.imprint","IMPRINT",FACE,{"disambiguationData":[TD([[makeQuery(id+"F2.imprint","IMPRINT",EDGE,{"derivedFrom":sQuery(id+"F2.wireOp",EDGE,"E21.7.0.34")}),1.0]])]});
            var Q102;
            Q102=makeQuery(id+"F2.imprint","IMPRINT",FACE,{"disambiguationData":[TD([[makeQuery(id+"F2.imprint","IMPRINT",EDGE,{"derivedFrom":sQuery(id+"F2.wireOp",EDGE,"E21.1.0.31")}),-1.0]])]});
            var Q103;
            {var subQ0=sQuery(id+"F2.wireOp",EDGE,"E21.6.0.45");Q103=makeQuery(id+"F2.imprint","IMPRINT",FACE,{"disambiguationData":[TD([[makeQuery(id+"F2.imprint","IMPRINT",EDGE,{"derivedFrom":subQ0}),1.0]])]});}
            var Q104;
            {var subQ0=sQuery(id+"F2.wireOp",EDGE,"E21.4.0.33");Q104=makeQuery(id+"F2.imprint","IMPRINT",FACE,{"disambiguationData":[TD([[makeQuery(id+"F2.imprint","IMPRINT",EDGE,{"derivedFrom":subQ0}),-1.0]])]});}
            var Q105;
            Q105=makeQuery(id+"F2.imprint","IMPRINT",FACE,{"disambiguationData":[TD([[makeQuery(id+"F2.imprint","IMPRINT",EDGE,{"derivedFrom":sQuery(id+"F2.wireOp",EDGE,"E21.5.0.31")}),-1.0]])]});
            var Q106;
            {var subQ0=sQuery(id+"F2.wireOp",EDGE,"E21.1.0.33");Q106=makeQuery(id+"F2.imprint","IMPRINT",FACE,{"disambiguationData":[TD([[makeQuery(id+"F2.imprint","IMPRINT",EDGE,{"derivedFrom":subQ0}),-1.0]])]});}
            var Q107;
            Q107=makeQuery(id+"F2.imprint","IMPRINT",FACE,{"disambiguationData":[TD([[makeQuery(id+"F2.imprint","IMPRINT",EDGE,{"derivedFrom":sQuery(id+"F2.wireOp",EDGE,"E18.bottom")}),-1.0]])]});
            var Q108;
            Q108=makeQuery(id+"F2.imprint","IMPRINT",FACE,{"disambiguationData":[TD([[makeQuery(id+"F2.imprint","IMPRINT",EDGE,{"derivedFrom":sQuery(id+"F2.wireOp",EDGE,"E21.5.0.30")}),-1.0]])]});
            var Q109;
            {var subQ0=sQuery(id+"F2.wireOp",EDGE,"E21.4.0.9");Q109=makeQuery(id+"F2.imprint","IMPRINT",FACE,{"disambiguationData":[TD([[makeQuery(id+"F2.imprint","IMPRINT",EDGE,{"derivedFrom":subQ0}),-1.0]])]});}
            var Q110;
            Q110=makeQuery(id+"F2.imprint","IMPRINT",FACE,{"disambiguationData":[TD([[makeQuery(id+"F2.imprint","IMPRINT",EDGE,{"derivedFrom":sQuery(id+"F2.wireOp",EDGE,"E21.7.0.30")}),-1.0]])]});
            var Q111;
            Q111=makeQuery(id+"F2.imprint","IMPRINT",FACE,{"disambiguationData":[TD([[makeQuery(id+"F2.imprint","IMPRINT",EDGE,{"derivedFrom":sQuery(id+"F2.wireOp",EDGE,"E21.5.0.34")}),1.0]])]});
            var Q112;
            Q112=makeQuery(id+"F2.imprint","IMPRINT",FACE,{"disambiguationData":[TD([[makeQuery(id+"F2.imprint","IMPRINT",EDGE,{"derivedFrom":sQuery(id+"F2.wireOp",EDGE,"E21.6.0.30")}),-1.0]])]});
            var Q113;
            {var subQ0=sQuery(id+"F2.wireOp",EDGE,"E21.4.0.45");Q113=makeQuery(id+"F2.imprint","IMPRINT",FACE,{"disambiguationData":[TD([[makeQuery(id+"F2.imprint","IMPRINT",EDGE,{"derivedFrom":subQ0}),1.0]])]});}
            var Q114;
            Q114=makeQuery(id+"F2.imprint","IMPRINT",FACE,{"disambiguationData":[TD([[makeQuery(id+"F2.imprint","IMPRINT",EDGE,{"derivedFrom":sQuery(id+"F2.wireOp",EDGE,"E21.4.0.31")}),-1.0]])]});
            var Q115;
            Q115=makeQuery(id+"F2.imprint","IMPRINT",FACE,{"disambiguationData":[TD([[makeQuery(id+"F2.imprint","IMPRINT",EDGE,{"derivedFrom":sQuery(id+"F2.wireOp",EDGE,"E21.3.0.30")}),-1.0]])]});
            var Q116;
            Q116=makeQuery(id+"F2.imprint","IMPRINT",FACE,{"disambiguationData":[TD([[makeQuery(id+"F2.imprint","IMPRINT",EDGE,{"derivedFrom":sQuery(id+"F2.wireOp",EDGE,"E21.2.0.30")}),-1.0]])]});
            var Q117;
            {var subQ0=sQuery(id+"F2.wireOp",EDGE,"E21.3.0.33");Q117=makeQuery(id+"F2.imprint","IMPRINT",FACE,{"disambiguationData":[TD([[makeQuery(id+"F2.imprint","IMPRINT",EDGE,{"derivedFrom":subQ0}),-1.0]])]});}
            var Q118;
            Q118=makeQuery(id+"F2.imprint","IMPRINT",FACE,{"disambiguationData":[TD([[makeQuery(id+"F2.imprint","IMPRINT",EDGE,{"derivedFrom":sQuery(id+"F2.wireOp",EDGE,"E21.6.0.31")}),-1.0]])]});
            var Q119;
            Q119=makeQuery(id+"F2.imprint","IMPRINT",FACE,{"disambiguationData":[TD([[makeQuery(id+"F2.imprint","IMPRINT",EDGE,{"derivedFrom":sQuery(id+"F2.wireOp",EDGE,"E21.1.0.34")}),1.0]])]});
            var Q120;
            Q120=makeQuery(id+"F2.imprint","IMPRINT",FACE,{"disambiguationData":[TD([[makeQuery(id+"F2.imprint","IMPRINT",EDGE,{"derivedFrom":sQuery(id+"F2.wireOp",EDGE,"E21.6.0.34")}),1.0]])]});
            var Q121;
            Q121=makeQuery(id+"F2.imprint","IMPRINT",FACE,{"disambiguationData":[TD([[makeQuery(id+"F2.imprint","IMPRINT",EDGE,{"derivedFrom":sQuery(id+"F2.wireOp",EDGE,"E21.3.0.31")}),-1.0]])]});
            var Q122;
            Q122=makeQuery(id+"F2.imprint","IMPRINT",FACE,{"disambiguationData":[TD([[makeQuery(id+"F2.imprint","IMPRINT",EDGE,{"derivedFrom":sQuery(id+"F2.wireOp",EDGE,"E21.2.0.34")}),1.0]])]});
            var Q123;
            Q123=makeQuery(id+"F2.imprint","IMPRINT",FACE,{"disambiguationData":[TD([[makeQuery(id+"F2.imprint","IMPRINT",EDGE,{"derivedFrom":sQuery(id+"F2.wireOp",EDGE,"E21.4.0.34")}),1.0]])]});
            var Q124;
            Q124=makeQuery(id+"F2.imprint","IMPRINT",FACE,{"disambiguationData":[TD([[makeQuery(id+"F2.imprint","IMPRINT",EDGE,{"derivedFrom":sQuery(id+"F2.wireOp",EDGE,"E20.bottom")}),-1.0]])]});
            var Q125;
            {var subQ0=sQuery(id+"F2.wireOp",EDGE,"E21.2.0.33");Q125=makeQuery(id+"F2.imprint","IMPRINT",FACE,{"disambiguationData":[TD([[makeQuery(id+"F2.imprint","IMPRINT",EDGE,{"derivedFrom":subQ0}),-1.0]])]});}
            var Q126;
            {var subQ0=sQuery(id+"F2.wireOp",EDGE,"E19.bottom");Q126=makeQuery(id+"F2.imprint","IMPRINT",FACE,{"disambiguationData":[TD([[makeQuery(id+"F2.imprint","IMPRINT",EDGE,{"derivedFrom":subQ0}),-1.0]])]});}
            var Q127;
            {var subQ0=sQuery(id+"F2.wireOp",EDGE,"E21.2.0.45");Q127=makeQuery(id+"F2.imprint","IMPRINT",FACE,{"disambiguationData":[TD([[makeQuery(id+"F2.imprint","IMPRINT",EDGE,{"derivedFrom":subQ0}),1.0]])]});}
            var Q128;
            Q128=makeQuery(id+"F2.imprint","IMPRINT",FACE,{"disambiguationData":[TD([[makeQuery(id+"F2.imprint","IMPRINT",EDGE,{"derivedFrom":sQuery(id+"F2.wireOp",EDGE,"E17.bottom")}),-1.0]])]});
            var Q129;
            Q129=makeQuery(id+"F2.imprint","IMPRINT",FACE,{"disambiguationData":[TD([[makeQuery(id+"F2.imprint","IMPRINT",EDGE,{"derivedFrom":sQuery(id+"F2.wireOp",EDGE,"E21.3.0.34")}),1.0]])]});
            var Q130;
            {var subQ0=sQuery(id+"F2.wireOp",EDGE,"E21.7.0.33");Q130=makeQuery(id+"F2.imprint","IMPRINT",FACE,{"disambiguationData":[TD([[makeQuery(id+"F2.imprint","IMPRINT",EDGE,{"derivedFrom":subQ0}),-1.0]])]});}
            var Q131;
            {var subQ0=sQuery(id+"F2.wireOp",EDGE,"E21.7.0.45");Q131=makeQuery(id+"F2.imprint","IMPRINT",FACE,{"disambiguationData":[TD([[makeQuery(id+"F2.imprint","IMPRINT",EDGE,{"derivedFrom":subQ0}),1.0]])]});}
            var Q132;
            {var subQ0=sQuery(id+"F2.wireOp",EDGE,"E19.top");Q132=makeQuery(id+"F2.imprint","IMPRINT",FACE,{"disambiguationData":[TD([[makeQuery(id+"F2.imprint","IMPRINT",EDGE,{"derivedFrom":subQ0}),1.0]])]});}
            extrude(context, id + "F3", {"entities" : qUnion([Q0, Q1, Q2, Q3, Q4, Q5, Q6, Q7, Q8, Q9, Q10, Q11, Q12, Q13, Q14, Q15, Q16, Q17, Q18, Q19, Q20, Q21, Q22, Q23, Q24, Q25, Q26, Q27, Q28, Q29, Q30, Q31, Q32, Q33, Q34, Q35, Q36, Q37, Q38, Q39, Q40, Q41, Q42, Q43, Q44, Q45, Q46, Q47, Q48, Q49, Q50, Q51, Q52, Q53, Q54, Q55, Q56, Q57, Q58, Q59, Q60, Q61, Q62, Q63, Q64, Q65, Q66, Q67, Q68, Q69, Q70, Q71, Q72, Q73, Q74, Q75, Q76, Q77, Q78, Q79, Q80, Q81, Q82, Q83, Q84, Q85, Q86, Q87, Q88, Q89, Q90, Q91, Q92, Q93, Q94, Q95, Q96, Q97, Q98, Q99, Q100, Q101, Q102, Q103, Q104, Q105, Q106, Q107, Q108, Q109, Q110, Q111, Q112, Q113, Q114, Q115, Q116, Q117, Q118, Q119, Q120, Q121, Q122, Q123, Q124, Q125, Q126, Q127, Q128, Q129, Q130, Q131, Q132]), "operationType" : NewBodyOperationType.ADD, "depth" : -1.2 * mm, "offsetDistance" : 25 * mm});
        }
        {
            var Q0;
            {var subQ3=sQuery(id+"F2.wireOp",EDGE,"E12.top");Q0=makeQuery(id+"F2.imprint","IMPRINT",FACE,{"disambiguationData":[TD([[makeQuery(id+"F2.imprint","IMPRINT",EDGE,{"derivedFrom":subQ3}),1.0]])]});}
            var Q1;
            {var subQ1=sQuery(id+"F2.wireOp",EDGE,"E10.top");Q1=makeQuery(id+"F2.imprint","IMPRINT",FACE,{"disambiguationData":[TD([[makeQuery(id+"F2.imprint","IMPRINT",EDGE,{"derivedFrom":subQ1}),-1.0]])]});}
            var Q2;
            {var subQ1=sQuery(id+"F2.wireOp",EDGE,"E9.top");Q2=makeQuery(id+"F2.imprint","IMPRINT",FACE,{"disambiguationData":[TD([[makeQuery(id+"F2.imprint","IMPRINT",EDGE,{"derivedFrom":subQ1}),-1.0]])]});}
            var Q3;
            {var subQ0=sQuery(id+"F2.wireOp",EDGE,"E10.top");Q3=makeQuery(id+"F2.imprint","IMPRINT",FACE,{"disambiguationData":[TD([[makeQuery(id+"F2.imprint","IMPRINT",EDGE,{"derivedFrom":subQ0}),1.0]])]});}
            var Q4;
            {var subQ1=sQuery(id+"F2.wireOp",EDGE,"E9.top");Q4=makeQuery(id+"F2.imprint","IMPRINT",FACE,{"disambiguationData":[TD([[makeQuery(id+"F2.imprint","IMPRINT",EDGE,{"derivedFrom":subQ1}),1.0]])]});}
            var Q5;
            {var subQ0=sQuery(id+"F2.wireOp",EDGE,"E19.bottom");Q5=makeQuery(id+"F2.imprint","IMPRINT",FACE,{"disambiguationData":[TD([[makeQuery(id+"F2.imprint","IMPRINT",EDGE,{"derivedFrom":subQ0}),1.0]])]});}
            var Q6;
            {var subQ5=sQuery(id+"F2.wireOp",EDGE,"E21.1.0.8");Q6=makeQuery(id+"F2.imprint","IMPRINT",FACE,{"disambiguationData":[TD([[makeQuery(id+"F2.imprint","IMPRINT",EDGE,{"derivedFrom":subQ5}),1.0]])]});}
            var Q7;
            {var subQ0=sQuery(id+"F2.wireOp",EDGE,"E21.1.0.33");Q7=makeQuery(id+"F2.imprint","IMPRINT",FACE,{"disambiguationData":[TD([[makeQuery(id+"F2.imprint","IMPRINT",EDGE,{"derivedFrom":subQ0}),1.0]])]});}
            var Q8;
            {var subQ1=sQuery(id+"F2.wireOp",EDGE,"E21.1.0.8");Q8=makeQuery(id+"F2.imprint","IMPRINT",FACE,{"disambiguationData":[TD([[makeQuery(id+"F2.imprint","IMPRINT",EDGE,{"derivedFrom":subQ1}),-1.0]])]});}
            var Q9;
            Q9=makeQuery(id+"F2.imprint","IMPRINT",FACE,{"disambiguationData":[TD([[makeQuery(id+"F2.imprint","IMPRINT",EDGE,{"derivedFrom":sQuery(id+"F2.wireOp",EDGE,"E21.1.0.5")}),-1.0]])]});
            var Q10;
            {var subQ1=sQuery(id+"F2.wireOp",EDGE,"E21.1.0.0");Q10=makeQuery(id+"F2.imprint","IMPRINT",FACE,{"disambiguationData":[TD([[makeQuery(id+"F2.imprint","IMPRINT",EDGE,{"derivedFrom":subQ1}),-1.0]])]});}
            var Q11;
            {var subQ1=sQuery(id+"F2.wireOp",EDGE,"E21.2.0.0");Q11=makeQuery(id+"F2.imprint","IMPRINT",FACE,{"disambiguationData":[TD([[makeQuery(id+"F2.imprint","IMPRINT",EDGE,{"derivedFrom":subQ1}),-1.0]])]});}
            var Q12;
            Q12=makeQuery(id+"F2.imprint","IMPRINT",FACE,{"disambiguationData":[TD([[makeQuery(id+"F2.imprint","IMPRINT",EDGE,{"derivedFrom":sQuery(id+"F2.wireOp",EDGE,"E21.2.0.5")}),-1.0]])]});
            var Q13;
            {var subQ5=sQuery(id+"F2.wireOp",EDGE,"E21.2.0.5");Q13=makeQuery(id+"F2.imprint","IMPRINT",FACE,{"disambiguationData":[TD([[makeQuery(id+"F2.imprint","IMPRINT",EDGE,{"derivedFrom":subQ5}),1.0]])]});}
            var Q14;
            {var subQ5=sQuery(id+"F2.wireOp",EDGE,"E21.2.0.8");Q14=makeQuery(id+"F2.imprint","IMPRINT",FACE,{"disambiguationData":[TD([[makeQuery(id+"F2.imprint","IMPRINT",EDGE,{"derivedFrom":subQ5}),1.0]])]});}
            var Q15;
            {var subQ1=sQuery(id+"F2.wireOp",EDGE,"E21.1.0.5");Q15=makeQuery(id+"F2.imprint","IMPRINT",FACE,{"disambiguationData":[TD([[makeQuery(id+"F2.imprint","IMPRINT",EDGE,{"derivedFrom":subQ1}),1.0]])]});}
            var Q16;
            {var subQ0=sQuery(id+"F2.wireOp",EDGE,"E21.2.0.33");Q16=makeQuery(id+"F2.imprint","IMPRINT",FACE,{"disambiguationData":[TD([[makeQuery(id+"F2.imprint","IMPRINT",EDGE,{"derivedFrom":subQ0}),1.0]])]});}
            var Q17;
            {var subQ1=sQuery(id+"F2.wireOp",EDGE,"E21.2.0.8");Q17=makeQuery(id+"F2.imprint","IMPRINT",FACE,{"disambiguationData":[TD([[makeQuery(id+"F2.imprint","IMPRINT",EDGE,{"derivedFrom":subQ1}),-1.0]])]});}
            var Q18;
            {var subQ0=sQuery(id+"F2.wireOp",EDGE,"E21.3.0.33");Q18=makeQuery(id+"F2.imprint","IMPRINT",FACE,{"disambiguationData":[TD([[makeQuery(id+"F2.imprint","IMPRINT",EDGE,{"derivedFrom":subQ0}),1.0]])]});}
            var Q19;
            {var subQ5=sQuery(id+"F2.wireOp",EDGE,"E21.3.0.8");Q19=makeQuery(id+"F2.imprint","IMPRINT",FACE,{"disambiguationData":[TD([[makeQuery(id+"F2.imprint","IMPRINT",EDGE,{"derivedFrom":subQ5}),1.0]])]});}
            var Q20;
            {var subQ1=sQuery(id+"F2.wireOp",EDGE,"E21.3.0.5");Q20=makeQuery(id+"F2.imprint","IMPRINT",FACE,{"disambiguationData":[TD([[makeQuery(id+"F2.imprint","IMPRINT",EDGE,{"derivedFrom":subQ1}),1.0]])]});}
            var Q21;
            Q21=makeQuery(id+"F2.imprint","IMPRINT",FACE,{"disambiguationData":[TD([[makeQuery(id+"F2.imprint","IMPRINT",EDGE,{"derivedFrom":sQuery(id+"F2.wireOp",EDGE,"E21.3.0.5")}),-1.0]])]});
            var Q22;
            {var subQ1=sQuery(id+"F2.wireOp",EDGE,"E21.5.0.0");Q22=makeQuery(id+"F2.imprint","IMPRINT",FACE,{"disambiguationData":[TD([[makeQuery(id+"F2.imprint","IMPRINT",EDGE,{"derivedFrom":subQ1}),-1.0]])]});}
            var Q23;
            {var subQ1=sQuery(id+"F2.wireOp",EDGE,"E21.6.0.0");Q23=makeQuery(id+"F2.imprint","IMPRINT",FACE,{"disambiguationData":[TD([[makeQuery(id+"F2.imprint","IMPRINT",EDGE,{"derivedFrom":subQ1}),-1.0]])]});}
            var Q24;
            {var subQ0=sQuery(id+"F2.wireOp",EDGE,"E21.7.0.0");Q24=makeQuery(id+"F2.imprint","IMPRINT",FACE,{"disambiguationData":[TD([[makeQuery(id+"F2.imprint","IMPRINT",EDGE,{"derivedFrom":subQ0}),-1.0]])]});}
            var Q25;
            Q25=makeQuery(id+"F2.imprint","IMPRINT",FACE,{"disambiguationData":[TD([[makeQuery(id+"F2.imprint","IMPRINT",EDGE,{"derivedFrom":sQuery(id+"F2.wireOp",EDGE,"E21.5.0.5")}),-1.0]])]});
            var Q26;
            Q26=makeQuery(id+"F2.imprint","IMPRINT",FACE,{"disambiguationData":[TD([[makeQuery(id+"F2.imprint","IMPRINT",EDGE,{"derivedFrom":sQuery(id+"F2.wireOp",EDGE,"E21.6.0.5")}),-1.0]])]});
            var Q27;
            Q27=makeQuery(id+"F2.imprint","IMPRINT",FACE,{"disambiguationData":[TD([[makeQuery(id+"F2.imprint","IMPRINT",EDGE,{"derivedFrom":sQuery(id+"F2.wireOp",EDGE,"E21.7.0.5")}),-1.0]])]});
            var Q28;
            {var subQ1=sQuery(id+"F2.wireOp",EDGE,"E21.5.0.5");Q28=makeQuery(id+"F2.imprint","IMPRINT",FACE,{"disambiguationData":[TD([[makeQuery(id+"F2.imprint","IMPRINT",EDGE,{"derivedFrom":subQ1}),1.0]])]});}
            var Q29;
            Q29=makeQuery(id+"F2.imprint","IMPRINT",FACE,{"disambiguationData":[TD([[makeQuery(id+"F2.imprint","IMPRINT",EDGE,{"derivedFrom":sQuery(id+"F2.wireOp",EDGE,"E21.4.0.5")}),-1.0]])]});
            var Q30;
            {var subQ1=sQuery(id+"F2.wireOp",EDGE,"E21.4.0.5");Q30=makeQuery(id+"F2.imprint","IMPRINT",FACE,{"disambiguationData":[TD([[makeQuery(id+"F2.imprint","IMPRINT",EDGE,{"derivedFrom":subQ1}),1.0]])]});}
            var Q31;
            {var subQ1=sQuery(id+"F2.wireOp",EDGE,"E21.4.0.8");Q31=makeQuery(id+"F2.imprint","IMPRINT",FACE,{"disambiguationData":[TD([[makeQuery(id+"F2.imprint","IMPRINT",EDGE,{"derivedFrom":subQ1}),-1.0]])]});}
            var Q32;
            {var subQ6=sQuery(id+"F2.wireOp",EDGE,"E21.4.0.8");Q32=makeQuery(id+"F2.imprint","IMPRINT",FACE,{"disambiguationData":[TD([[makeQuery(id+"F2.imprint","IMPRINT",EDGE,{"derivedFrom":subQ6}),1.0]])]});}
            var Q33;
            {var subQ0=sQuery(id+"F2.wireOp",EDGE,"E21.4.0.33");Q33=makeQuery(id+"F2.imprint","IMPRINT",FACE,{"disambiguationData":[TD([[makeQuery(id+"F2.imprint","IMPRINT",EDGE,{"derivedFrom":subQ0}),1.0]])]});}
            var Q34;
            {var subQ0=sQuery(id+"F2.wireOp",EDGE,"E21.5.0.33");Q34=makeQuery(id+"F2.imprint","IMPRINT",FACE,{"disambiguationData":[TD([[makeQuery(id+"F2.imprint","IMPRINT",EDGE,{"derivedFrom":subQ0}),1.0]])]});}
            var Q35;
            {var subQ1=sQuery(id+"F2.wireOp",EDGE,"E21.5.0.8");Q35=makeQuery(id+"F2.imprint","IMPRINT",FACE,{"disambiguationData":[TD([[makeQuery(id+"F2.imprint","IMPRINT",EDGE,{"derivedFrom":subQ1}),-1.0]])]});}
            var Q36;
            {var subQ5=sQuery(id+"F2.wireOp",EDGE,"E21.5.0.8");Q36=makeQuery(id+"F2.imprint","IMPRINT",FACE,{"disambiguationData":[TD([[makeQuery(id+"F2.imprint","IMPRINT",EDGE,{"derivedFrom":subQ5}),1.0]])]});}
            var Q37;
            {var subQ1=sQuery(id+"F2.wireOp",EDGE,"E21.6.0.8");Q37=makeQuery(id+"F2.imprint","IMPRINT",FACE,{"disambiguationData":[TD([[makeQuery(id+"F2.imprint","IMPRINT",EDGE,{"derivedFrom":subQ1}),-1.0]])]});}
            var Q38;
            {var subQ1=sQuery(id+"F2.wireOp",EDGE,"E21.6.0.5");Q38=makeQuery(id+"F2.imprint","IMPRINT",FACE,{"disambiguationData":[TD([[makeQuery(id+"F2.imprint","IMPRINT",EDGE,{"derivedFrom":subQ1}),1.0]])]});}
            var Q39;
            {var subQ5=sQuery(id+"F2.wireOp",EDGE,"E21.6.0.8");Q39=makeQuery(id+"F2.imprint","IMPRINT",FACE,{"disambiguationData":[TD([[makeQuery(id+"F2.imprint","IMPRINT",EDGE,{"derivedFrom":subQ5}),1.0]])]});}
            var Q40;
            {var subQ0=sQuery(id+"F2.wireOp",EDGE,"E21.6.0.33");Q40=makeQuery(id+"F2.imprint","IMPRINT",FACE,{"disambiguationData":[TD([[makeQuery(id+"F2.imprint","IMPRINT",EDGE,{"derivedFrom":subQ0}),1.0]])]});}
            var Q41;
            {var subQ0=sQuery(id+"F2.wireOp",EDGE,"E21.7.0.33");Q41=makeQuery(id+"F2.imprint","IMPRINT",FACE,{"disambiguationData":[TD([[makeQuery(id+"F2.imprint","IMPRINT",EDGE,{"derivedFrom":subQ0}),1.0]])]});}
            var Q42;
            {var subQ5=sQuery(id+"F2.wireOp",EDGE,"E21.7.0.8");Q42=makeQuery(id+"F2.imprint","IMPRINT",FACE,{"disambiguationData":[TD([[makeQuery(id+"F2.imprint","IMPRINT",EDGE,{"derivedFrom":subQ5}),1.0]])]});}
            var Q43;
            {var subQ1=sQuery(id+"F2.wireOp",EDGE,"E21.7.0.8");Q43=makeQuery(id+"F2.imprint","IMPRINT",FACE,{"disambiguationData":[TD([[makeQuery(id+"F2.imprint","IMPRINT",EDGE,{"derivedFrom":subQ1}),-1.0]])]});}
            var Q44;
            {var subQ1=sQuery(id+"F2.wireOp",EDGE,"E21.7.0.5");Q44=makeQuery(id+"F2.imprint","IMPRINT",FACE,{"disambiguationData":[TD([[makeQuery(id+"F2.imprint","IMPRINT",EDGE,{"derivedFrom":subQ1}),1.0]])]});}
            var Q45;
            {var subQ1=sQuery(id+"F2.wireOp",EDGE,"E21.3.0.8");Q45=makeQuery(id+"F2.imprint","IMPRINT",FACE,{"disambiguationData":[TD([[makeQuery(id+"F2.imprint","IMPRINT",EDGE,{"derivedFrom":subQ1}),-1.0]])]});}
            extrude(context, id + "F4", {"entities" : qUnion([Q0, Q1, Q2, Q3, Q4, Q5, Q6, Q7, Q8, Q9, Q10, Q11, Q12, Q13, Q14, Q15, Q16, Q17, Q18, Q19, Q20, Q21, Q22, Q23, Q24, Q25, Q26, Q27, Q28, Q29, Q30, Q31, Q32, Q33, Q34, Q35, Q36, Q37, Q38, Q39, Q40, Q41, Q42, Q43, Q44, Q45]), "operationType" : NewBodyOperationType.ADD, "depth" : 2.5 * mm, "offsetDistance" : 25 * mm});
        }
        {
            var Q0;
            Q0=makeQuery(id+"F2.imprint","IMPRINT",FACE,{"disambiguationData":[TD([[makeQuery(id+"F2.imprint","IMPRINT",EDGE,{"derivedFrom":sQuery(id+"F2.wireOp",EDGE,"E21.7.0.34")}),1.0]])]});
            var Q1;
            Q1=makeQuery(id+"F2.imprint","IMPRINT",FACE,{"disambiguationData":[TD([[makeQuery(id+"F2.imprint","IMPRINT",EDGE,{"derivedFrom":sQuery(id+"F2.wireOp",EDGE,"E21.6.0.34")}),1.0]])]});
            var Q2;
            Q2=makeQuery(id+"F2.imprint","IMPRINT",FACE,{"disambiguationData":[TD([[makeQuery(id+"F2.imprint","IMPRINT",EDGE,{"derivedFrom":sQuery(id+"F2.wireOp",EDGE,"E21.5.0.34")}),1.0]])]});
            var Q3;
            Q3=makeQuery(id+"F2.imprint","IMPRINT",FACE,{"disambiguationData":[TD([[makeQuery(id+"F2.imprint","IMPRINT",EDGE,{"derivedFrom":sQuery(id+"F2.wireOp",EDGE,"E21.5.0.31")}),-1.0]])]});
            var Q4;
            Q4=makeQuery(id+"F2.imprint","IMPRINT",FACE,{"disambiguationData":[TD([[makeQuery(id+"F2.imprint","IMPRINT",EDGE,{"derivedFrom":sQuery(id+"F2.wireOp",EDGE,"E21.6.0.31")}),-1.0]])]});
            var Q5;
            Q5=makeQuery(id+"F2.imprint","IMPRINT",FACE,{"disambiguationData":[TD([[makeQuery(id+"F2.imprint","IMPRINT",EDGE,{"derivedFrom":sQuery(id+"F2.wireOp",EDGE,"E21.7.0.31")}),-1.0]])]});
            var Q6;
            Q6=makeQuery(id+"F2.imprint","IMPRINT",FACE,{"disambiguationData":[TD([[makeQuery(id+"F2.imprint","IMPRINT",EDGE,{"derivedFrom":sQuery(id+"F2.wireOp",EDGE,"E21.7.0.30")}),-1.0]])]});
            var Q7;
            Q7=makeQuery(id+"F2.imprint","IMPRINT",FACE,{"disambiguationData":[TD([[makeQuery(id+"F2.imprint","IMPRINT",EDGE,{"derivedFrom":sQuery(id+"F2.wireOp",EDGE,"E21.6.0.30")}),-1.0]])]});
            var Q8;
            Q8=makeQuery(id+"F2.imprint","IMPRINT",FACE,{"disambiguationData":[TD([[makeQuery(id+"F2.imprint","IMPRINT",EDGE,{"derivedFrom":sQuery(id+"F2.wireOp",EDGE,"E21.5.0.30")}),-1.0]])]});
            var Q9;
            {var subQ0=sQuery(id+"F2.wireOp",EDGE,"E21.5.0.33");Q9=makeQuery(id+"F2.imprint","IMPRINT",FACE,{"disambiguationData":[TD([[makeQuery(id+"F2.imprint","IMPRINT",EDGE,{"derivedFrom":subQ0}),-1.0]])]});}
            var Q10;
            {var subQ0=sQuery(id+"F2.wireOp",EDGE,"E21.6.0.33");Q10=makeQuery(id+"F2.imprint","IMPRINT",FACE,{"disambiguationData":[TD([[makeQuery(id+"F2.imprint","IMPRINT",EDGE,{"derivedFrom":subQ0}),-1.0]])]});}
            var Q11;
            {var subQ0=sQuery(id+"F2.wireOp",EDGE,"E21.7.0.33");Q11=makeQuery(id+"F2.imprint","IMPRINT",FACE,{"disambiguationData":[TD([[makeQuery(id+"F2.imprint","IMPRINT",EDGE,{"derivedFrom":subQ0}),-1.0]])]});}
            var Q12;
            {var subQ0=sQuery(id+"F2.wireOp",EDGE,"E21.6.0.45");Q12=makeQuery(id+"F2.imprint","IMPRINT",FACE,{"disambiguationData":[TD([[makeQuery(id+"F2.imprint","IMPRINT",EDGE,{"derivedFrom":subQ0}),1.0]])]});}
            var Q13;
            {var subQ0=sQuery(id+"F2.wireOp",EDGE,"E21.5.0.45");Q13=makeQuery(id+"F2.imprint","IMPRINT",FACE,{"disambiguationData":[TD([[makeQuery(id+"F2.imprint","IMPRINT",EDGE,{"derivedFrom":subQ0}),1.0]])]});}
            var Q14;
            {var subQ0=sQuery(id+"F2.wireOp",EDGE,"E21.7.0.45");Q14=makeQuery(id+"F2.imprint","IMPRINT",FACE,{"disambiguationData":[TD([[makeQuery(id+"F2.imprint","IMPRINT",EDGE,{"derivedFrom":subQ0}),1.0]])]});}
            var Q15;
            {var subQ0=sQuery(id+"F2.wireOp",EDGE,"E21.4.0.33");Q15=makeQuery(id+"F2.imprint","IMPRINT",FACE,{"disambiguationData":[TD([[makeQuery(id+"F2.imprint","IMPRINT",EDGE,{"derivedFrom":subQ0}),-1.0]])]});}
            var Q16;
            {var subQ0=sQuery(id+"F2.wireOp",EDGE,"E21.4.0.45");Q16=makeQuery(id+"F2.imprint","IMPRINT",FACE,{"disambiguationData":[TD([[makeQuery(id+"F2.imprint","IMPRINT",EDGE,{"derivedFrom":subQ0}),1.0]])]});}
            var Q17;
            Q17=makeQuery(id+"F2.imprint","IMPRINT",FACE,{"disambiguationData":[TD([[makeQuery(id+"F2.imprint","IMPRINT",EDGE,{"derivedFrom":sQuery(id+"F2.wireOp",EDGE,"E21.4.0.30")}),-1.0]])]});
            var Q18;
            Q18=makeQuery(id+"F2.imprint","IMPRINT",FACE,{"disambiguationData":[TD([[makeQuery(id+"F2.imprint","IMPRINT",EDGE,{"derivedFrom":sQuery(id+"F2.wireOp",EDGE,"E21.4.0.31")}),-1.0]])]});
            var Q19;
            Q19=makeQuery(id+"F2.imprint","IMPRINT",FACE,{"disambiguationData":[TD([[makeQuery(id+"F2.imprint","IMPRINT",EDGE,{"derivedFrom":sQuery(id+"F2.wireOp",EDGE,"E21.2.0.34")}),1.0]])]});
            var Q20;
            Q20=makeQuery(id+"F2.imprint","IMPRINT",FACE,{"disambiguationData":[TD([[makeQuery(id+"F2.imprint","IMPRINT",EDGE,{"derivedFrom":sQuery(id+"F2.wireOp",EDGE,"E21.1.0.34")}),1.0]])]});
            var Q21;
            Q21=makeQuery(id+"F2.imprint","IMPRINT",FACE,{"disambiguationData":[TD([[makeQuery(id+"F2.imprint","IMPRINT",EDGE,{"derivedFrom":sQuery(id+"F2.wireOp",EDGE,"E20.bottom")}),-1.0]])]});
            var Q22;
            Q22=makeQuery(id+"F2.imprint","IMPRINT",FACE,{"disambiguationData":[TD([[makeQuery(id+"F2.imprint","IMPRINT",EDGE,{"derivedFrom":sQuery(id+"F2.wireOp",EDGE,"E17.bottom")}),-1.0]])]});
            var Q23;
            Q23=makeQuery(id+"F2.imprint","IMPRINT",FACE,{"disambiguationData":[TD([[makeQuery(id+"F2.imprint","IMPRINT",EDGE,{"derivedFrom":sQuery(id+"F2.wireOp",EDGE,"E21.1.0.31")}),-1.0]])]});
            var Q24;
            Q24=makeQuery(id+"F2.imprint","IMPRINT",FACE,{"disambiguationData":[TD([[makeQuery(id+"F2.imprint","IMPRINT",EDGE,{"derivedFrom":sQuery(id+"F2.wireOp",EDGE,"E21.2.0.31")}),-1.0]])]});
            var Q25;
            Q25=makeQuery(id+"F2.imprint","IMPRINT",FACE,{"disambiguationData":[TD([[makeQuery(id+"F2.imprint","IMPRINT",EDGE,{"derivedFrom":sQuery(id+"F2.wireOp",EDGE,"E21.3.0.31")}),-1.0]])]});
            var Q26;
            Q26=makeQuery(id+"F2.imprint","IMPRINT",FACE,{"disambiguationData":[TD([[makeQuery(id+"F2.imprint","IMPRINT",EDGE,{"derivedFrom":sQuery(id+"F2.wireOp",EDGE,"E21.3.0.30")}),-1.0]])]});
            var Q27;
            Q27=makeQuery(id+"F2.imprint","IMPRINT",FACE,{"disambiguationData":[TD([[makeQuery(id+"F2.imprint","IMPRINT",EDGE,{"derivedFrom":sQuery(id+"F2.wireOp",EDGE,"E21.2.0.30")}),-1.0]])]});
            var Q28;
            Q28=makeQuery(id+"F2.imprint","IMPRINT",FACE,{"disambiguationData":[TD([[makeQuery(id+"F2.imprint","IMPRINT",EDGE,{"derivedFrom":sQuery(id+"F2.wireOp",EDGE,"E21.1.0.30")}),-1.0]])]});
            var Q29;
            Q29=makeQuery(id+"F2.imprint","IMPRINT",FACE,{"disambiguationData":[TD([[makeQuery(id+"F2.imprint","IMPRINT",EDGE,{"derivedFrom":sQuery(id+"F2.wireOp",EDGE,"E18.bottom")}),-1.0]])]});
            var Q30;
            {var subQ0=sQuery(id+"F2.wireOp",EDGE,"E19.bottom");Q30=makeQuery(id+"F2.imprint","IMPRINT",FACE,{"disambiguationData":[TD([[makeQuery(id+"F2.imprint","IMPRINT",EDGE,{"derivedFrom":subQ0}),-1.0]])]});}
            var Q31;
            {var subQ0=sQuery(id+"F2.wireOp",EDGE,"E19.top");Q31=makeQuery(id+"F2.imprint","IMPRINT",FACE,{"disambiguationData":[TD([[makeQuery(id+"F2.imprint","IMPRINT",EDGE,{"derivedFrom":subQ0}),1.0]])]});}
            var Q32;
            {var subQ0=sQuery(id+"F2.wireOp",EDGE,"E21.1.0.33");Q32=makeQuery(id+"F2.imprint","IMPRINT",FACE,{"disambiguationData":[TD([[makeQuery(id+"F2.imprint","IMPRINT",EDGE,{"derivedFrom":subQ0}),-1.0]])]});}
            var Q33;
            {var subQ0=sQuery(id+"F2.wireOp",EDGE,"E21.2.0.33");Q33=makeQuery(id+"F2.imprint","IMPRINT",FACE,{"disambiguationData":[TD([[makeQuery(id+"F2.imprint","IMPRINT",EDGE,{"derivedFrom":subQ0}),-1.0]])]});}
            var Q34;
            {var subQ0=sQuery(id+"F2.wireOp",EDGE,"E21.3.0.33");Q34=makeQuery(id+"F2.imprint","IMPRINT",FACE,{"disambiguationData":[TD([[makeQuery(id+"F2.imprint","IMPRINT",EDGE,{"derivedFrom":subQ0}),-1.0]])]});}
            var Q35;
            {var subQ0=sQuery(id+"F2.wireOp",EDGE,"E21.3.0.45");Q35=makeQuery(id+"F2.imprint","IMPRINT",FACE,{"disambiguationData":[TD([[makeQuery(id+"F2.imprint","IMPRINT",EDGE,{"derivedFrom":subQ0}),1.0]])]});}
            var Q36;
            {var subQ0=sQuery(id+"F2.wireOp",EDGE,"E21.2.0.45");Q36=makeQuery(id+"F2.imprint","IMPRINT",FACE,{"disambiguationData":[TD([[makeQuery(id+"F2.imprint","IMPRINT",EDGE,{"derivedFrom":subQ0}),1.0]])]});}
            var Q37;
            {var subQ0=sQuery(id+"F2.wireOp",EDGE,"E21.1.0.45");Q37=makeQuery(id+"F2.imprint","IMPRINT",FACE,{"disambiguationData":[TD([[makeQuery(id+"F2.imprint","IMPRINT",EDGE,{"derivedFrom":subQ0}),1.0]])]});}
            extrude(context, id + "F5", {"entities" : qUnion([Q0, Q1, Q2, Q3, Q4, Q5, Q6, Q7, Q8, Q9, Q10, Q11, Q12, Q13, Q14, Q15, Q16, Q17, Q18, Q19, Q20, Q21, Q22, Q23, Q24, Q25, Q26, Q27, Q28, Q29, Q30, Q31, Q32, Q33, Q34, Q35, Q36, Q37]), "operationType" : NewBodyOperationType.ADD, "depth" : 8.6 * mm, "offsetDistance" : 25 * mm});
        }
        {
            var Q0;
            Q0=makeQuery(id+"F0.imprint","IMPRINT",FACE,{"disambiguationData":[TD([[makeQuery(id+"F0.imprint","IMPRINT",EDGE,{"derivedFrom":sQuery(id+"F0.wireOp",EDGE,"E1.bottom")}),-1.0]])]});
            extrude(context, id + "F6", {"entities" : qUnion([Q0]), "operationType" : NewBodyOperationType.ADD, "depth" : 5 * mm, "offsetDistance" : 25 * mm});
        }
        {
            var Q0;
            Q0=makeQuery(id+"F0.imprint","IMPRINT",FACE,{"disambiguationData":[TD([[makeQuery(id+"F0.imprint","IMPRINT",EDGE,{"derivedFrom":sQuery(id+"F0.wireOp",EDGE,"E0.bottom")}),1.0]])]});
            var sketch = newSketch(context, id + "F7", { "sketchPlane" : qUnion([Q0])});
            skLineSegment(sketch, "E22.0", {"start": v(0, 23.4) * mm, "end": v(36.1, 23.4) * mm});
            skLineSegment(sketch, "E23.0.0", {"start": v(36.1, 23.4) * mm, "end": v(0, 23.4) * mm});
            skLineSegment(sketch, "E23.0.1", {"start": v(0, 23.4) * mm, "end": v(0, 0) * mm});
            skLineSegment(sketch, "E23.0.2", {"start": v(0, 0) * mm, "end": v(36.1, 0) * mm});
            skLineSegment(sketch, "E23.0.3", {"start": v(36.1, 0) * mm, "end": v(36.1, 23.4) * mm});
            skLineSegment(sketch, "E24.bottom", {"start": v(30.1, 21.4) * mm, "end": v(27.6, 21.4) * mm});
            skLineSegment(sketch, "E24.top", {"start": v(30.1, 13.9) * mm, "end": v(27.6, 13.9) * mm});
            skLineSegment(sketch, "E24.left", {"start": v(30.1, 21.4) * mm, "end": v(30.1, 13.9) * mm});
            skLineSegment(sketch, "E24.right", {"start": v(27.6, 21.4) * mm, "end": v(27.6, 13.9) * mm});
            skLineSegment(sketch, "E25.bottom", {"start": v(32.15, 11.25) * mm, "end": v(34.65, 11.25) * mm});
            skLineSegment(sketch, "E25.top", {"start": v(32.15, 6.75) * mm, "end": v(34.65, 6.75) * mm});
            skLineSegment(sketch, "E25.left", {"start": v(32.15, 11.25) * mm, "end": v(32.15, 6.75) * mm});
            skLineSegment(sketch, "E25.right", {"start": v(34.65, 11.25) * mm, "end": v(34.65, 6.75) * mm});
            skPoint(sketch, "E25.middle", {"position": v(33.4, 9) * mm});
            skSolve(sketch);
        }
        {
            var Q0;
            {var subQ0=sQuery(id+"F7.wireOp",EDGE,"E24.right");Q0=makeQuery(id+"F7.imprint","IMPRINT",FACE,{"disambiguationData":[TD([[makeQuery(id+"F7.imprint","IMPRINT",EDGE,{"derivedFrom":subQ0}),1.0]])]});}
            var Q1;
            {var subQ0=sQuery(id+"F7.wireOp",EDGE,"E24.left");Q1=makeQuery(id+"F7.imprint","IMPRINT",FACE,{"disambiguationData":[TD([[makeQuery(id+"F7.imprint","IMPRINT",EDGE,{"derivedFrom":subQ0}),-1.0]])]});}
            extrude(context, id + "F8", {"entities" : qUnion([Q0, Q1]), "operationType" : NewBodyOperationType.ADD, "depth" : -2.5 * mm, "offsetDistance" : 25 * mm});
        }
        {
            var Q0;
            Q0=makeQuery(id+"F8.opExtrude","SWEPT_FACE",FACE,{"disambiguationData":[OSD([sQuery(id+"F7.wireOp",EDGE,"E24.left")])]});
            var sketch = newSketch(context, id + "F9", { "sketchPlane" : qUnion([Q0])});
            skLineSegment(sketch, "E26", {"start": v(13.9, 0) * mm, "end": v(16.4, 0) * mm});
            skLineSegment(sketch, "E27", {"start": v(16.4, 0) * mm, "end": v(18.9, 0) * mm});
            skLineSegment(sketch, "E28", {"start": v(18.9, 0) * mm, "end": v(21.4, 0) * mm});
            skLineSegment(sketch, "E29", {"start": v(16.4, 0) * mm, "end": v(16.4, -2.5) * mm});
            skLineSegment(sketch, "E30", {"start": v(18.9, 0) * mm, "end": v(18.9, -2.5) * mm});
            skLineSegment(sketch, "E31", {"start": v(13.9, -1.25) * mm, "end": v(16.4, -1.25) * mm, "construction": true});
            skLineSegment(sketch, "E32", {"start": v(16.4, -1.25) * mm, "end": v(18.9, -1.25) * mm, "construction": true});
            skLineSegment(sketch, "E33", {"start": v(18.9, -1.25) * mm, "end": v(21.4, -1.25) * mm, "construction": true});
            skLineSegment(sketch, "E34.bottom", {"start": v(15.45, -1.55) * mm, "end": v(14.85, -1.55) * mm});
            skLineSegment(sketch, "E34.top", {"start": v(15.45, -0.95) * mm, "end": v(14.85, -0.95) * mm});
            skLineSegment(sketch, "E34.left", {"start": v(15.45, -1.55) * mm, "end": v(15.45, -0.95) * mm});
            skLineSegment(sketch, "E34.right", {"start": v(14.85, -1.55) * mm, "end": v(14.85, -0.95) * mm});
            skPoint(sketch, "E34.middle", {"position": v(15.15, -1.25) * mm});
            skLineSegment(sketch, "E35.bottom", {"start": v(17.95, -1.55) * mm, "end": v(17.35, -1.55) * mm});
            skLineSegment(sketch, "E35.top", {"start": v(17.95, -0.95) * mm, "end": v(17.35, -0.95) * mm});
            skLineSegment(sketch, "E35.left", {"start": v(17.95, -1.55) * mm, "end": v(17.95, -0.95) * mm});
            skLineSegment(sketch, "E35.right", {"start": v(17.35, -1.55) * mm, "end": v(17.35, -0.95) * mm});
            skPoint(sketch, "E35.middle", {"position": v(17.65, -1.25) * mm});
            skLineSegment(sketch, "E36.bottom", {"start": v(20.45, -1.55) * mm, "end": v(19.85, -1.55) * mm});
            skLineSegment(sketch, "E36.top", {"start": v(20.45, -0.95) * mm, "end": v(19.85, -0.95) * mm});
            skLineSegment(sketch, "E36.left", {"start": v(20.45, -1.55) * mm, "end": v(20.45, -0.95) * mm});
            skLineSegment(sketch, "E36.right", {"start": v(19.85, -1.55) * mm, "end": v(19.85, -0.95) * mm});
            skPoint(sketch, "E36.middle", {"position": v(20.15, -1.25) * mm});
            skSolve(sketch);
        }
        {
            var Q0;
            Q0=makeQuery(id+"F9.imprint","IMPRINT",FACE,{"disambiguationData":[TD([[makeQuery(id+"F9.imprint","IMPRINT",EDGE,{"derivedFrom":sQuery(id+"F9.wireOp",EDGE,"E34.bottom")}),-1.0]])]});
            var Q1;
            Q1=makeQuery(id+"F9.imprint","IMPRINT",FACE,{"disambiguationData":[TD([[makeQuery(id+"F9.imprint","IMPRINT",EDGE,{"derivedFrom":sQuery(id+"F9.wireOp",EDGE,"E35.bottom")}),-1.0]])]});
            var Q2;
            Q2=makeQuery(id+"F9.imprint","IMPRINT",FACE,{"disambiguationData":[TD([[makeQuery(id+"F9.imprint","IMPRINT",EDGE,{"derivedFrom":sQuery(id+"F9.wireOp",EDGE,"E36.bottom")}),-1.0]])]});
            extrude(context, id + "F10", {"entities" : qUnion([Q0, Q1, Q2]), "operationType" : NewBodyOperationType.ADD, "depth" : 6 * mm, "offsetDistance" : 25 * mm});
        }
        {
            var Q0;
            Q0=makeQuery(id+"F7.imprint","IMPRINT",FACE,{"disambiguationData":[TD([[makeQuery(id+"F7.imprint","IMPRINT",EDGE,{"derivedFrom":sQuery(id+"F7.wireOp",EDGE,"E25.bottom")}),-1.0]])]});
            extrude(context, id + "F11", {"entities" : qUnion([Q0]), "operationType" : NewBodyOperationType.ADD, "depth" : -1.5 * mm, "offsetDistance" : 25 * mm});
        }
    });
